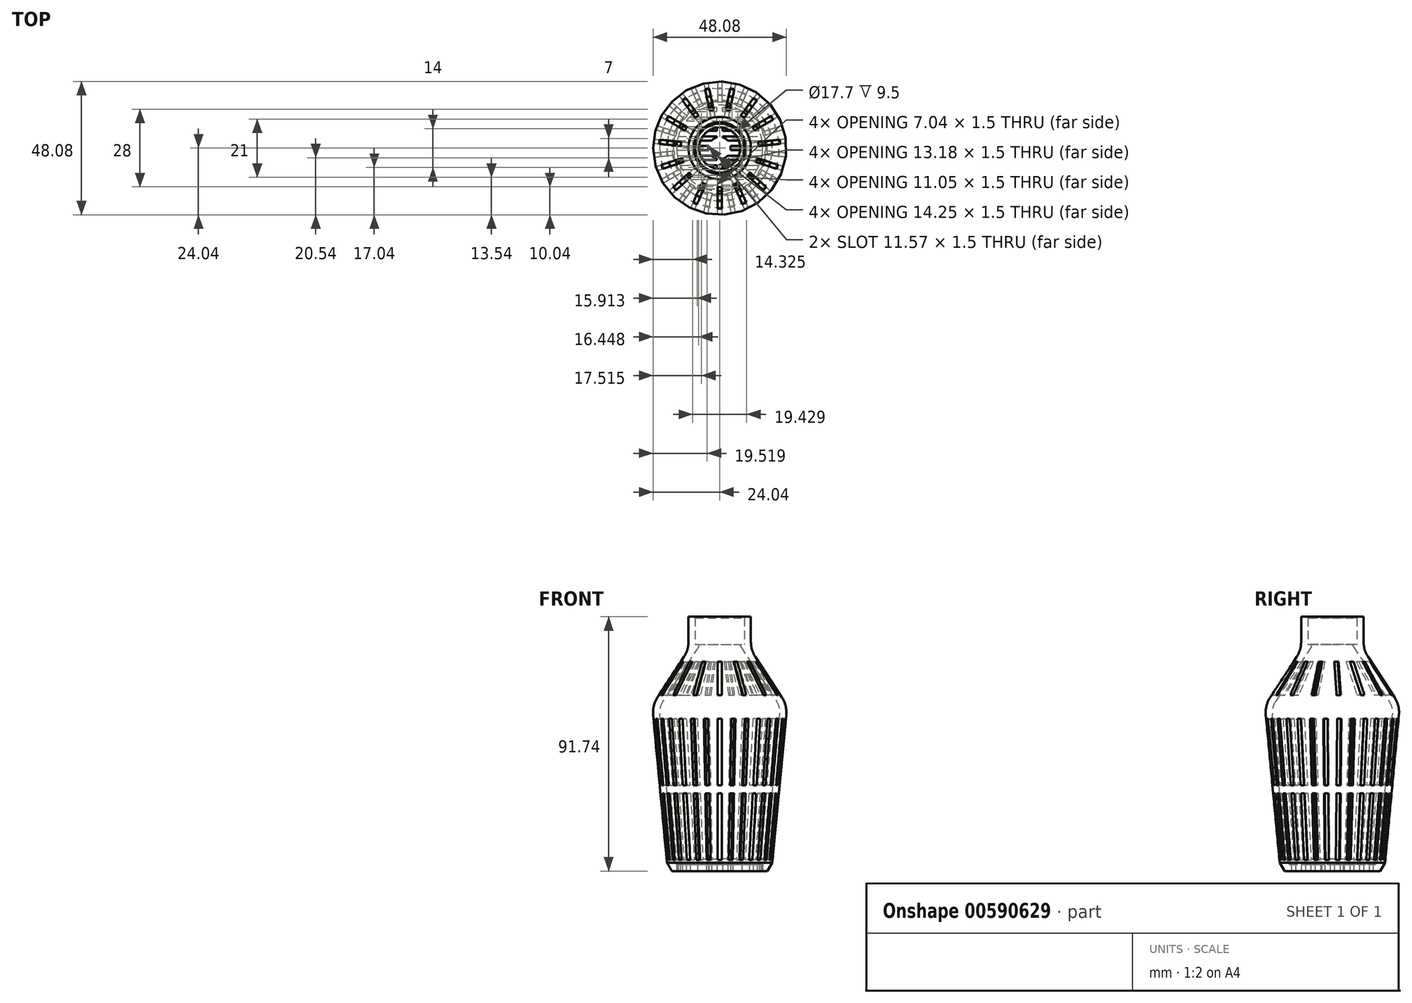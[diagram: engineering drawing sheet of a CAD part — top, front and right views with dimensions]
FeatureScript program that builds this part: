
annotation { "Feature Type Name" : "Feature", "Feature Type Description" : "" }
export const myFeature = defineFeature(function(context is Context, id is Id, definition is map)
    precondition{}
    {
        {
            var Q0;
            Q0=qCreatedBy(makeId("Front.planeOp"),FACE);
            var sketch = newSketch(context, id + "F0", { "sketchPlane" : qUnion([Q0])});
            skLineSegment(sketch, "E0", {"start": v(0, 0) * mm, "end": v(0, 100) * mm, "construction": true});
            skLineSegment(sketch, "E1", {"start": v(0, 0) * mm, "end": v(17.21, 0) * mm});
            skLineSegment(sketch, "E2", {"start": v(19, 3) * mm, "end": v(24, 56.26) * mm});
            skLineSegment(sketch, "E3", {"start": v(22.41, 62.66) * mm, "end": v(12.88, 77.24) * mm});
            skLineSegment(sketch, "E4", {"start": v(11.25, 82.72) * mm, "end": v(11.25, 91.74) * mm});
            skPoint(sketch, "E5.visualSharp", {"position": v(11.25, 79.74) * mm});
            skArc(sketch, "E5.filletArc", {"start": v(11.25, 82.72) * mm, "mid": v(11.67, 79.86) * mm, "end": v(12.88, 77.24) * mm});
            skPoint(sketch, "E6.visualSharp", {"position": v(24.33, 59.74) * mm});
            skArc(sketch, "E6.filletArc", {"start": v(24, 56.26) * mm, "mid": v(23.75, 59.6) * mm, "end": v(22.41, 62.66) * mm});
            skLineSegment(sketch, "E7", {"start": v(17.21, 0) * mm, "end": v(19, 3) * mm});
            skPoint(sketch, "E8.orphan", {"position": v(18.72, 0) * mm});
            skLineSegment(sketch, "E9.0", {"start": v(8.85, 81.74) * mm, "end": v(8.85, 91.74) * mm});
            skLineSegment(sketch, "E9.2", {"start": v(0, 2.4) * mm, "end": v(15.53, 2.4) * mm});
            skLineSegment(sketch, "E9.3", {"start": v(16.72, 4.4) * mm, "end": v(21.61, 56.48) * mm});
            skArc(sketch, "E9.4", {"start": v(21.61, 56.48) * mm, "mid": v(21.42, 59.02) * mm, "end": v(20.4, 61.35) * mm});
            skLineSegment(sketch, "E9.5", {"start": v(20.4, 61.35) * mm, "end": v(7.58, 80.96) * mm});
            skLineSegment(sketch, "E10", {"start": v(8.85, 91.74) * mm, "end": v(11.25, 91.74) * mm});
            skLineSegment(sketch, "E11", {"start": v(0, 2.4) * mm, "end": v(0, 0) * mm});
            skLineSegment(sketch, "E12", {"start": v(15.53, 2.4) * mm, "end": v(16.72, 4.4) * mm});
            skLineSegment(sketch, "E13", {"start": v(8.85, 81.74) * mm, "end": v(8, 81.74) * mm});
            skPoint(sketch, "E14.visualSharp", {"position": v(7.07, 81.74) * mm});
            skArc(sketch, "E14.filletArc", {"start": v(8, 81.74) * mm, "mid": v(7.56, 81.48) * mm, "end": v(7.58, 80.96) * mm});
            skSolve(sketch);
        }
        {
            var Q0;
            Q0 = qSketchRegion(id + "F0", true);
            var Q1;
            Q1=sQuery(id+"F0.wireOp",EDGE,"E0");
            revolve(context, id + "F1", {"entities" : qUnion([Q0]), "axis" : qUnion([Q1]), "revolveType" : RevolveType.FULL});
        }
        {
            var Q0;
            Q0=qCreatedBy(makeId("Front.planeOp"),FACE);
            var sketch = newSketch(context, id + "F2", { "sketchPlane" : qUnion([Q0])});
            skLineSegment(sketch, "E15", {"start": v(0, 0) * mm, "end": v(0, 100) * mm, "construction": true});
            skLineSegment(sketch, "E16.bottom", {"start": v(0.75, 4) * mm, "end": v(-0.75, 4) * mm});
            skLineSegment(sketch, "E16.top", {"start": v(0.75, 28) * mm, "end": v(-0.75, 28) * mm});
            skLineSegment(sketch, "E16.left", {"start": v(0.75, 4) * mm, "end": v(0.75, 28) * mm});
            skLineSegment(sketch, "E16.right", {"start": v(-0.75, 4) * mm, "end": v(-0.75, 28) * mm});
            skPoint(sketch, "E16.middle", {"position": v(0, 16) * mm});
            skLineSegment(sketch, "E17.bottom", {"start": v(0.75, 31) * mm, "end": v(-0.75, 31) * mm});
            skLineSegment(sketch, "E17.top", {"start": v(0.75, 55) * mm, "end": v(-0.75, 55) * mm});
            skLineSegment(sketch, "E17.left", {"start": v(0.75, 31) * mm, "end": v(0.75, 55) * mm});
            skLineSegment(sketch, "E17.right", {"start": v(-0.75, 31) * mm, "end": v(-0.75, 55) * mm});
            skPoint(sketch, "E17.middle", {"position": v(0, 43) * mm});
            skSolve(sketch);
        }
        {
            var Q0;
            Q0 = qSketchRegion(id + "F2", true);
            extrude(context, id + "F3", {"entities" : qUnion([Q0]), "oppositeDirection" : true, "depth" : 30 * mm, "offsetDistance" : 25 * mm});
        }
        {
            var Q0;
            Q0=makeQuery(id+"F3.opExtrude","SWEPT_BODY",BODY,{"disambiguationData":[OSD([sQuery(id+"F2.wireOp",EDGE,"E16.bottom"),sQuery(id+"F2.wireOp",EDGE,"E16.top"),sQuery(id+"F2.wireOp",EDGE,"E16.left"),sQuery(id+"F2.wireOp",EDGE,"E16.right")])]});
            var Q1;
            Q1=makeQuery(id+"F3.opExtrude","SWEPT_BODY",BODY,{"disambiguationData":[OSD([sQuery(id+"F2.wireOp",EDGE,"E17.bottom"),sQuery(id+"F2.wireOp",EDGE,"E17.top"),sQuery(id+"F2.wireOp",EDGE,"E17.left"),sQuery(id+"F2.wireOp",EDGE,"E17.right")])]});
            var Q2;
            Q2=makeQuery(id+"F3.opExtrude","SWEPT_BODY",BODY,{"disambiguationData":[OSD([sQuery(id+"F2.wireOp",EDGE,"CUWT8K6s-WbJc-WrEz-pjmn-ECC45j0oT72r.bottom"),sQuery(id+"F2.wireOp",EDGE,"CUWT8K6s-WbJc-WrEz-pjmn-ECC45j0oT72r.top"),sQuery(id+"F2.wireOp",EDGE,"CUWT8K6s-WbJc-WrEz-pjmn-ECC45j0oT72r.left"),sQuery(id+"F2.wireOp",EDGE,"CUWT8K6s-WbJc-WrEz-pjmn-ECC45j0oT72r.right")])]});
            var Q3;
            Q3=sQuery(id+"F0.wireOp",EDGE,"E0");
            circularPattern(context, id + "F4", {"entities" : qUnion([Q0, Q1, Q2]), "axis" : qUnion([Q3]), "angle" : 360 * degree, "instanceCount" : 30, "equalSpace" : true});
        }
        {
            var Q0;
            Q0=makeQuery(id+"F3.opExtrude","SWEPT_BODY",BODY,{"disambiguationData":[OSD([sQuery(id+"F2.wireOp",EDGE,"E16.bottom"),sQuery(id+"F2.wireOp",EDGE,"E16.top"),sQuery(id+"F2.wireOp",EDGE,"E16.left"),sQuery(id+"F2.wireOp",EDGE,"E16.right")])]});
            var Q1;
            Q1=makeQuery(id+"F3.opExtrude","SWEPT_BODY",BODY,{"disambiguationData":[OSD([sQuery(id+"F2.wireOp",EDGE,"E17.bottom"),sQuery(id+"F2.wireOp",EDGE,"E17.top"),sQuery(id+"F2.wireOp",EDGE,"E17.left"),sQuery(id+"F2.wireOp",EDGE,"E17.right")])]});
            var Q2;
            Q2=makeQuery(id+"F3.opExtrude","SWEPT_BODY",BODY,{"disambiguationData":[OSD([sQuery(id+"F2.wireOp",EDGE,"CUWT8K6s-WbJc-WrEz-pjmn-ECC45j0oT72r.bottom"),sQuery(id+"F2.wireOp",EDGE,"CUWT8K6s-WbJc-WrEz-pjmn-ECC45j0oT72r.top"),sQuery(id+"F2.wireOp",EDGE,"CUWT8K6s-WbJc-WrEz-pjmn-ECC45j0oT72r.left"),sQuery(id+"F2.wireOp",EDGE,"CUWT8K6s-WbJc-WrEz-pjmn-ECC45j0oT72r.right")])]});
            var Q3;
            Q3=makeQuery(id+"F4.opPattern","COPY",BODY,{"derivedFrom":makeQuery(id+"F3.opExtrude","SWEPT_BODY",BODY,{"disambiguationData":[OSD([sQuery(id+"F2.wireOp",EDGE,"E16.bottom"),sQuery(id+"F2.wireOp",EDGE,"E16.top"),sQuery(id+"F2.wireOp",EDGE,"E16.left"),sQuery(id+"F2.wireOp",EDGE,"E16.right")])]}),"instanceName":"1"});
            var Q4;
            Q4=makeQuery(id+"F4.opPattern","COPY",BODY,{"derivedFrom":makeQuery(id+"F3.opExtrude","SWEPT_BODY",BODY,{"disambiguationData":[OSD([sQuery(id+"F2.wireOp",EDGE,"E17.bottom"),sQuery(id+"F2.wireOp",EDGE,"E17.top"),sQuery(id+"F2.wireOp",EDGE,"E17.left"),sQuery(id+"F2.wireOp",EDGE,"E17.right")])]}),"instanceName":"1"});
            var Q5;
            Q5=makeQuery(id+"F4.opPattern","COPY",BODY,{"derivedFrom":makeQuery(id+"F3.opExtrude","SWEPT_BODY",BODY,{"disambiguationData":[OSD([sQuery(id+"F2.wireOp",EDGE,"CUWT8K6s-WbJc-WrEz-pjmn-ECC45j0oT72r.bottom"),sQuery(id+"F2.wireOp",EDGE,"CUWT8K6s-WbJc-WrEz-pjmn-ECC45j0oT72r.top"),sQuery(id+"F2.wireOp",EDGE,"CUWT8K6s-WbJc-WrEz-pjmn-ECC45j0oT72r.left"),sQuery(id+"F2.wireOp",EDGE,"CUWT8K6s-WbJc-WrEz-pjmn-ECC45j0oT72r.right")])]}),"instanceName":"1"});
            var Q6;
            Q6=makeQuery(id+"F4.opPattern","COPY",BODY,{"derivedFrom":makeQuery(id+"F3.opExtrude","SWEPT_BODY",BODY,{"disambiguationData":[OSD([sQuery(id+"F2.wireOp",EDGE,"E16.bottom"),sQuery(id+"F2.wireOp",EDGE,"E16.top"),sQuery(id+"F2.wireOp",EDGE,"E16.left"),sQuery(id+"F2.wireOp",EDGE,"E16.right")])]}),"instanceName":"2"});
            var Q7;
            Q7=makeQuery(id+"F4.opPattern","COPY",BODY,{"derivedFrom":makeQuery(id+"F3.opExtrude","SWEPT_BODY",BODY,{"disambiguationData":[OSD([sQuery(id+"F2.wireOp",EDGE,"E17.bottom"),sQuery(id+"F2.wireOp",EDGE,"E17.top"),sQuery(id+"F2.wireOp",EDGE,"E17.left"),sQuery(id+"F2.wireOp",EDGE,"E17.right")])]}),"instanceName":"2"});
            var Q8;
            Q8=makeQuery(id+"F4.opPattern","COPY",BODY,{"derivedFrom":makeQuery(id+"F3.opExtrude","SWEPT_BODY",BODY,{"disambiguationData":[OSD([sQuery(id+"F2.wireOp",EDGE,"CUWT8K6s-WbJc-WrEz-pjmn-ECC45j0oT72r.bottom"),sQuery(id+"F2.wireOp",EDGE,"CUWT8K6s-WbJc-WrEz-pjmn-ECC45j0oT72r.top"),sQuery(id+"F2.wireOp",EDGE,"CUWT8K6s-WbJc-WrEz-pjmn-ECC45j0oT72r.left"),sQuery(id+"F2.wireOp",EDGE,"CUWT8K6s-WbJc-WrEz-pjmn-ECC45j0oT72r.right")])]}),"instanceName":"2"});
            var Q9;
            Q9=makeQuery(id+"F4.opPattern","COPY",BODY,{"derivedFrom":makeQuery(id+"F3.opExtrude","SWEPT_BODY",BODY,{"disambiguationData":[OSD([sQuery(id+"F2.wireOp",EDGE,"E16.bottom"),sQuery(id+"F2.wireOp",EDGE,"E16.top"),sQuery(id+"F2.wireOp",EDGE,"E16.left"),sQuery(id+"F2.wireOp",EDGE,"E16.right")])]}),"instanceName":"3"});
            var Q10;
            Q10=makeQuery(id+"F4.opPattern","COPY",BODY,{"derivedFrom":makeQuery(id+"F3.opExtrude","SWEPT_BODY",BODY,{"disambiguationData":[OSD([sQuery(id+"F2.wireOp",EDGE,"E17.bottom"),sQuery(id+"F2.wireOp",EDGE,"E17.top"),sQuery(id+"F2.wireOp",EDGE,"E17.left"),sQuery(id+"F2.wireOp",EDGE,"E17.right")])]}),"instanceName":"3"});
            var Q11;
            Q11=makeQuery(id+"F4.opPattern","COPY",BODY,{"derivedFrom":makeQuery(id+"F3.opExtrude","SWEPT_BODY",BODY,{"disambiguationData":[OSD([sQuery(id+"F2.wireOp",EDGE,"CUWT8K6s-WbJc-WrEz-pjmn-ECC45j0oT72r.bottom"),sQuery(id+"F2.wireOp",EDGE,"CUWT8K6s-WbJc-WrEz-pjmn-ECC45j0oT72r.top"),sQuery(id+"F2.wireOp",EDGE,"CUWT8K6s-WbJc-WrEz-pjmn-ECC45j0oT72r.left"),sQuery(id+"F2.wireOp",EDGE,"CUWT8K6s-WbJc-WrEz-pjmn-ECC45j0oT72r.right")])]}),"instanceName":"3"});
            var Q12;
            Q12=makeQuery(id+"F4.opPattern","COPY",BODY,{"derivedFrom":makeQuery(id+"F3.opExtrude","SWEPT_BODY",BODY,{"disambiguationData":[OSD([sQuery(id+"F2.wireOp",EDGE,"E16.bottom"),sQuery(id+"F2.wireOp",EDGE,"E16.top"),sQuery(id+"F2.wireOp",EDGE,"E16.left"),sQuery(id+"F2.wireOp",EDGE,"E16.right")])]}),"instanceName":"4"});
            var Q13;
            Q13=makeQuery(id+"F4.opPattern","COPY",BODY,{"derivedFrom":makeQuery(id+"F3.opExtrude","SWEPT_BODY",BODY,{"disambiguationData":[OSD([sQuery(id+"F2.wireOp",EDGE,"E17.bottom"),sQuery(id+"F2.wireOp",EDGE,"E17.top"),sQuery(id+"F2.wireOp",EDGE,"E17.left"),sQuery(id+"F2.wireOp",EDGE,"E17.right")])]}),"instanceName":"4"});
            var Q14;
            Q14=makeQuery(id+"F4.opPattern","COPY",BODY,{"derivedFrom":makeQuery(id+"F3.opExtrude","SWEPT_BODY",BODY,{"disambiguationData":[OSD([sQuery(id+"F2.wireOp",EDGE,"CUWT8K6s-WbJc-WrEz-pjmn-ECC45j0oT72r.bottom"),sQuery(id+"F2.wireOp",EDGE,"CUWT8K6s-WbJc-WrEz-pjmn-ECC45j0oT72r.top"),sQuery(id+"F2.wireOp",EDGE,"CUWT8K6s-WbJc-WrEz-pjmn-ECC45j0oT72r.left"),sQuery(id+"F2.wireOp",EDGE,"CUWT8K6s-WbJc-WrEz-pjmn-ECC45j0oT72r.right")])]}),"instanceName":"4"});
            var Q15;
            Q15=makeQuery(id+"F4.opPattern","COPY",BODY,{"derivedFrom":makeQuery(id+"F3.opExtrude","SWEPT_BODY",BODY,{"disambiguationData":[OSD([sQuery(id+"F2.wireOp",EDGE,"E16.bottom"),sQuery(id+"F2.wireOp",EDGE,"E16.top"),sQuery(id+"F2.wireOp",EDGE,"E16.left"),sQuery(id+"F2.wireOp",EDGE,"E16.right")])]}),"instanceName":"5"});
            var Q16;
            Q16=makeQuery(id+"F4.opPattern","COPY",BODY,{"derivedFrom":makeQuery(id+"F3.opExtrude","SWEPT_BODY",BODY,{"disambiguationData":[OSD([sQuery(id+"F2.wireOp",EDGE,"E17.bottom"),sQuery(id+"F2.wireOp",EDGE,"E17.top"),sQuery(id+"F2.wireOp",EDGE,"E17.left"),sQuery(id+"F2.wireOp",EDGE,"E17.right")])]}),"instanceName":"5"});
            var Q17;
            Q17=makeQuery(id+"F4.opPattern","COPY",BODY,{"derivedFrom":makeQuery(id+"F3.opExtrude","SWEPT_BODY",BODY,{"disambiguationData":[OSD([sQuery(id+"F2.wireOp",EDGE,"CUWT8K6s-WbJc-WrEz-pjmn-ECC45j0oT72r.bottom"),sQuery(id+"F2.wireOp",EDGE,"CUWT8K6s-WbJc-WrEz-pjmn-ECC45j0oT72r.top"),sQuery(id+"F2.wireOp",EDGE,"CUWT8K6s-WbJc-WrEz-pjmn-ECC45j0oT72r.left"),sQuery(id+"F2.wireOp",EDGE,"CUWT8K6s-WbJc-WrEz-pjmn-ECC45j0oT72r.right")])]}),"instanceName":"5"});
            var Q18;
            Q18=makeQuery(id+"F4.opPattern","COPY",BODY,{"derivedFrom":makeQuery(id+"F3.opExtrude","SWEPT_BODY",BODY,{"disambiguationData":[OSD([sQuery(id+"F2.wireOp",EDGE,"E16.bottom"),sQuery(id+"F2.wireOp",EDGE,"E16.top"),sQuery(id+"F2.wireOp",EDGE,"E16.left"),sQuery(id+"F2.wireOp",EDGE,"E16.right")])]}),"instanceName":"6"});
            var Q19;
            Q19=makeQuery(id+"F4.opPattern","COPY",BODY,{"derivedFrom":makeQuery(id+"F3.opExtrude","SWEPT_BODY",BODY,{"disambiguationData":[OSD([sQuery(id+"F2.wireOp",EDGE,"E17.bottom"),sQuery(id+"F2.wireOp",EDGE,"E17.top"),sQuery(id+"F2.wireOp",EDGE,"E17.left"),sQuery(id+"F2.wireOp",EDGE,"E17.right")])]}),"instanceName":"6"});
            var Q20;
            Q20=makeQuery(id+"F4.opPattern","COPY",BODY,{"derivedFrom":makeQuery(id+"F3.opExtrude","SWEPT_BODY",BODY,{"disambiguationData":[OSD([sQuery(id+"F2.wireOp",EDGE,"CUWT8K6s-WbJc-WrEz-pjmn-ECC45j0oT72r.bottom"),sQuery(id+"F2.wireOp",EDGE,"CUWT8K6s-WbJc-WrEz-pjmn-ECC45j0oT72r.top"),sQuery(id+"F2.wireOp",EDGE,"CUWT8K6s-WbJc-WrEz-pjmn-ECC45j0oT72r.left"),sQuery(id+"F2.wireOp",EDGE,"CUWT8K6s-WbJc-WrEz-pjmn-ECC45j0oT72r.right")])]}),"instanceName":"6"});
            var Q21;
            Q21=makeQuery(id+"F4.opPattern","COPY",BODY,{"derivedFrom":makeQuery(id+"F3.opExtrude","SWEPT_BODY",BODY,{"disambiguationData":[OSD([sQuery(id+"F2.wireOp",EDGE,"E16.bottom"),sQuery(id+"F2.wireOp",EDGE,"E16.top"),sQuery(id+"F2.wireOp",EDGE,"E16.left"),sQuery(id+"F2.wireOp",EDGE,"E16.right")])]}),"instanceName":"7"});
            var Q22;
            Q22=makeQuery(id+"F4.opPattern","COPY",BODY,{"derivedFrom":makeQuery(id+"F3.opExtrude","SWEPT_BODY",BODY,{"disambiguationData":[OSD([sQuery(id+"F2.wireOp",EDGE,"E17.bottom"),sQuery(id+"F2.wireOp",EDGE,"E17.top"),sQuery(id+"F2.wireOp",EDGE,"E17.left"),sQuery(id+"F2.wireOp",EDGE,"E17.right")])]}),"instanceName":"7"});
            var Q23;
            Q23=makeQuery(id+"F4.opPattern","COPY",BODY,{"derivedFrom":makeQuery(id+"F3.opExtrude","SWEPT_BODY",BODY,{"disambiguationData":[OSD([sQuery(id+"F2.wireOp",EDGE,"CUWT8K6s-WbJc-WrEz-pjmn-ECC45j0oT72r.bottom"),sQuery(id+"F2.wireOp",EDGE,"CUWT8K6s-WbJc-WrEz-pjmn-ECC45j0oT72r.top"),sQuery(id+"F2.wireOp",EDGE,"CUWT8K6s-WbJc-WrEz-pjmn-ECC45j0oT72r.left"),sQuery(id+"F2.wireOp",EDGE,"CUWT8K6s-WbJc-WrEz-pjmn-ECC45j0oT72r.right")])]}),"instanceName":"7"});
            var Q24;
            Q24=makeQuery(id+"F4.opPattern","COPY",BODY,{"derivedFrom":makeQuery(id+"F3.opExtrude","SWEPT_BODY",BODY,{"disambiguationData":[OSD([sQuery(id+"F2.wireOp",EDGE,"E16.bottom"),sQuery(id+"F2.wireOp",EDGE,"E16.top"),sQuery(id+"F2.wireOp",EDGE,"E16.left"),sQuery(id+"F2.wireOp",EDGE,"E16.right")])]}),"instanceName":"8"});
            var Q25;
            Q25=makeQuery(id+"F4.opPattern","COPY",BODY,{"derivedFrom":makeQuery(id+"F3.opExtrude","SWEPT_BODY",BODY,{"disambiguationData":[OSD([sQuery(id+"F2.wireOp",EDGE,"E17.bottom"),sQuery(id+"F2.wireOp",EDGE,"E17.top"),sQuery(id+"F2.wireOp",EDGE,"E17.left"),sQuery(id+"F2.wireOp",EDGE,"E17.right")])]}),"instanceName":"8"});
            var Q26;
            Q26=makeQuery(id+"F4.opPattern","COPY",BODY,{"derivedFrom":makeQuery(id+"F3.opExtrude","SWEPT_BODY",BODY,{"disambiguationData":[OSD([sQuery(id+"F2.wireOp",EDGE,"CUWT8K6s-WbJc-WrEz-pjmn-ECC45j0oT72r.bottom"),sQuery(id+"F2.wireOp",EDGE,"CUWT8K6s-WbJc-WrEz-pjmn-ECC45j0oT72r.top"),sQuery(id+"F2.wireOp",EDGE,"CUWT8K6s-WbJc-WrEz-pjmn-ECC45j0oT72r.left"),sQuery(id+"F2.wireOp",EDGE,"CUWT8K6s-WbJc-WrEz-pjmn-ECC45j0oT72r.right")])]}),"instanceName":"8"});
            var Q27;
            Q27=makeQuery(id+"F4.opPattern","COPY",BODY,{"derivedFrom":makeQuery(id+"F3.opExtrude","SWEPT_BODY",BODY,{"disambiguationData":[OSD([sQuery(id+"F2.wireOp",EDGE,"E16.bottom"),sQuery(id+"F2.wireOp",EDGE,"E16.top"),sQuery(id+"F2.wireOp",EDGE,"E16.left"),sQuery(id+"F2.wireOp",EDGE,"E16.right")])]}),"instanceName":"9"});
            var Q28;
            Q28=makeQuery(id+"F4.opPattern","COPY",BODY,{"derivedFrom":makeQuery(id+"F3.opExtrude","SWEPT_BODY",BODY,{"disambiguationData":[OSD([sQuery(id+"F2.wireOp",EDGE,"E17.bottom"),sQuery(id+"F2.wireOp",EDGE,"E17.top"),sQuery(id+"F2.wireOp",EDGE,"E17.left"),sQuery(id+"F2.wireOp",EDGE,"E17.right")])]}),"instanceName":"9"});
            var Q29;
            Q29=makeQuery(id+"F4.opPattern","COPY",BODY,{"derivedFrom":makeQuery(id+"F3.opExtrude","SWEPT_BODY",BODY,{"disambiguationData":[OSD([sQuery(id+"F2.wireOp",EDGE,"CUWT8K6s-WbJc-WrEz-pjmn-ECC45j0oT72r.bottom"),sQuery(id+"F2.wireOp",EDGE,"CUWT8K6s-WbJc-WrEz-pjmn-ECC45j0oT72r.top"),sQuery(id+"F2.wireOp",EDGE,"CUWT8K6s-WbJc-WrEz-pjmn-ECC45j0oT72r.left"),sQuery(id+"F2.wireOp",EDGE,"CUWT8K6s-WbJc-WrEz-pjmn-ECC45j0oT72r.right")])]}),"instanceName":"9"});
            var Q30;
            Q30=makeQuery(id+"F4.opPattern","COPY",BODY,{"derivedFrom":makeQuery(id+"F3.opExtrude","SWEPT_BODY",BODY,{"disambiguationData":[OSD([sQuery(id+"F2.wireOp",EDGE,"E16.bottom"),sQuery(id+"F2.wireOp",EDGE,"E16.top"),sQuery(id+"F2.wireOp",EDGE,"E16.left"),sQuery(id+"F2.wireOp",EDGE,"E16.right")])]}),"instanceName":"10"});
            var Q31;
            Q31=makeQuery(id+"F4.opPattern","COPY",BODY,{"derivedFrom":makeQuery(id+"F3.opExtrude","SWEPT_BODY",BODY,{"disambiguationData":[OSD([sQuery(id+"F2.wireOp",EDGE,"E17.bottom"),sQuery(id+"F2.wireOp",EDGE,"E17.top"),sQuery(id+"F2.wireOp",EDGE,"E17.left"),sQuery(id+"F2.wireOp",EDGE,"E17.right")])]}),"instanceName":"10"});
            var Q32;
            Q32=makeQuery(id+"F4.opPattern","COPY",BODY,{"derivedFrom":makeQuery(id+"F3.opExtrude","SWEPT_BODY",BODY,{"disambiguationData":[OSD([sQuery(id+"F2.wireOp",EDGE,"CUWT8K6s-WbJc-WrEz-pjmn-ECC45j0oT72r.bottom"),sQuery(id+"F2.wireOp",EDGE,"CUWT8K6s-WbJc-WrEz-pjmn-ECC45j0oT72r.top"),sQuery(id+"F2.wireOp",EDGE,"CUWT8K6s-WbJc-WrEz-pjmn-ECC45j0oT72r.left"),sQuery(id+"F2.wireOp",EDGE,"CUWT8K6s-WbJc-WrEz-pjmn-ECC45j0oT72r.right")])]}),"instanceName":"10"});
            var Q33;
            Q33=makeQuery(id+"F4.opPattern","COPY",BODY,{"derivedFrom":makeQuery(id+"F3.opExtrude","SWEPT_BODY",BODY,{"disambiguationData":[OSD([sQuery(id+"F2.wireOp",EDGE,"E16.bottom"),sQuery(id+"F2.wireOp",EDGE,"E16.top"),sQuery(id+"F2.wireOp",EDGE,"E16.left"),sQuery(id+"F2.wireOp",EDGE,"E16.right")])]}),"instanceName":"11"});
            var Q34;
            Q34=makeQuery(id+"F4.opPattern","COPY",BODY,{"derivedFrom":makeQuery(id+"F3.opExtrude","SWEPT_BODY",BODY,{"disambiguationData":[OSD([sQuery(id+"F2.wireOp",EDGE,"E17.bottom"),sQuery(id+"F2.wireOp",EDGE,"E17.top"),sQuery(id+"F2.wireOp",EDGE,"E17.left"),sQuery(id+"F2.wireOp",EDGE,"E17.right")])]}),"instanceName":"11"});
            var Q35;
            Q35=makeQuery(id+"F4.opPattern","COPY",BODY,{"derivedFrom":makeQuery(id+"F3.opExtrude","SWEPT_BODY",BODY,{"disambiguationData":[OSD([sQuery(id+"F2.wireOp",EDGE,"CUWT8K6s-WbJc-WrEz-pjmn-ECC45j0oT72r.bottom"),sQuery(id+"F2.wireOp",EDGE,"CUWT8K6s-WbJc-WrEz-pjmn-ECC45j0oT72r.top"),sQuery(id+"F2.wireOp",EDGE,"CUWT8K6s-WbJc-WrEz-pjmn-ECC45j0oT72r.left"),sQuery(id+"F2.wireOp",EDGE,"CUWT8K6s-WbJc-WrEz-pjmn-ECC45j0oT72r.right")])]}),"instanceName":"11"});
            var Q36;
            Q36=makeQuery(id+"F4.opPattern","COPY",BODY,{"derivedFrom":makeQuery(id+"F3.opExtrude","SWEPT_BODY",BODY,{"disambiguationData":[OSD([sQuery(id+"F2.wireOp",EDGE,"E16.bottom"),sQuery(id+"F2.wireOp",EDGE,"E16.top"),sQuery(id+"F2.wireOp",EDGE,"E16.left"),sQuery(id+"F2.wireOp",EDGE,"E16.right")])]}),"instanceName":"12"});
            var Q37;
            Q37=makeQuery(id+"F4.opPattern","COPY",BODY,{"derivedFrom":makeQuery(id+"F3.opExtrude","SWEPT_BODY",BODY,{"disambiguationData":[OSD([sQuery(id+"F2.wireOp",EDGE,"E17.bottom"),sQuery(id+"F2.wireOp",EDGE,"E17.top"),sQuery(id+"F2.wireOp",EDGE,"E17.left"),sQuery(id+"F2.wireOp",EDGE,"E17.right")])]}),"instanceName":"12"});
            var Q38;
            Q38=makeQuery(id+"F4.opPattern","COPY",BODY,{"derivedFrom":makeQuery(id+"F3.opExtrude","SWEPT_BODY",BODY,{"disambiguationData":[OSD([sQuery(id+"F2.wireOp",EDGE,"CUWT8K6s-WbJc-WrEz-pjmn-ECC45j0oT72r.bottom"),sQuery(id+"F2.wireOp",EDGE,"CUWT8K6s-WbJc-WrEz-pjmn-ECC45j0oT72r.top"),sQuery(id+"F2.wireOp",EDGE,"CUWT8K6s-WbJc-WrEz-pjmn-ECC45j0oT72r.left"),sQuery(id+"F2.wireOp",EDGE,"CUWT8K6s-WbJc-WrEz-pjmn-ECC45j0oT72r.right")])]}),"instanceName":"12"});
            var Q39;
            Q39=makeQuery(id+"F4.opPattern","COPY",BODY,{"derivedFrom":makeQuery(id+"F3.opExtrude","SWEPT_BODY",BODY,{"disambiguationData":[OSD([sQuery(id+"F2.wireOp",EDGE,"E16.bottom"),sQuery(id+"F2.wireOp",EDGE,"E16.top"),sQuery(id+"F2.wireOp",EDGE,"E16.left"),sQuery(id+"F2.wireOp",EDGE,"E16.right")])]}),"instanceName":"13"});
            var Q40;
            Q40=makeQuery(id+"F4.opPattern","COPY",BODY,{"derivedFrom":makeQuery(id+"F3.opExtrude","SWEPT_BODY",BODY,{"disambiguationData":[OSD([sQuery(id+"F2.wireOp",EDGE,"E17.bottom"),sQuery(id+"F2.wireOp",EDGE,"E17.top"),sQuery(id+"F2.wireOp",EDGE,"E17.left"),sQuery(id+"F2.wireOp",EDGE,"E17.right")])]}),"instanceName":"13"});
            var Q41;
            Q41=makeQuery(id+"F4.opPattern","COPY",BODY,{"derivedFrom":makeQuery(id+"F3.opExtrude","SWEPT_BODY",BODY,{"disambiguationData":[OSD([sQuery(id+"F2.wireOp",EDGE,"CUWT8K6s-WbJc-WrEz-pjmn-ECC45j0oT72r.bottom"),sQuery(id+"F2.wireOp",EDGE,"CUWT8K6s-WbJc-WrEz-pjmn-ECC45j0oT72r.top"),sQuery(id+"F2.wireOp",EDGE,"CUWT8K6s-WbJc-WrEz-pjmn-ECC45j0oT72r.left"),sQuery(id+"F2.wireOp",EDGE,"CUWT8K6s-WbJc-WrEz-pjmn-ECC45j0oT72r.right")])]}),"instanceName":"13"});
            var Q42;
            Q42=makeQuery(id+"F4.opPattern","COPY",BODY,{"derivedFrom":makeQuery(id+"F3.opExtrude","SWEPT_BODY",BODY,{"disambiguationData":[OSD([sQuery(id+"F2.wireOp",EDGE,"E16.bottom"),sQuery(id+"F2.wireOp",EDGE,"E16.top"),sQuery(id+"F2.wireOp",EDGE,"E16.left"),sQuery(id+"F2.wireOp",EDGE,"E16.right")])]}),"instanceName":"14"});
            var Q43;
            Q43=makeQuery(id+"F4.opPattern","COPY",BODY,{"derivedFrom":makeQuery(id+"F3.opExtrude","SWEPT_BODY",BODY,{"disambiguationData":[OSD([sQuery(id+"F2.wireOp",EDGE,"E17.bottom"),sQuery(id+"F2.wireOp",EDGE,"E17.top"),sQuery(id+"F2.wireOp",EDGE,"E17.left"),sQuery(id+"F2.wireOp",EDGE,"E17.right")])]}),"instanceName":"14"});
            var Q44;
            Q44=makeQuery(id+"F4.opPattern","COPY",BODY,{"derivedFrom":makeQuery(id+"F3.opExtrude","SWEPT_BODY",BODY,{"disambiguationData":[OSD([sQuery(id+"F2.wireOp",EDGE,"CUWT8K6s-WbJc-WrEz-pjmn-ECC45j0oT72r.bottom"),sQuery(id+"F2.wireOp",EDGE,"CUWT8K6s-WbJc-WrEz-pjmn-ECC45j0oT72r.top"),sQuery(id+"F2.wireOp",EDGE,"CUWT8K6s-WbJc-WrEz-pjmn-ECC45j0oT72r.left"),sQuery(id+"F2.wireOp",EDGE,"CUWT8K6s-WbJc-WrEz-pjmn-ECC45j0oT72r.right")])]}),"instanceName":"14"});
            var Q45;
            Q45=makeQuery(id+"F4.opPattern","COPY",BODY,{"derivedFrom":makeQuery(id+"F3.opExtrude","SWEPT_BODY",BODY,{"disambiguationData":[OSD([sQuery(id+"F2.wireOp",EDGE,"E16.bottom"),sQuery(id+"F2.wireOp",EDGE,"E16.top"),sQuery(id+"F2.wireOp",EDGE,"E16.left"),sQuery(id+"F2.wireOp",EDGE,"E16.right")])]}),"instanceName":"15"});
            var Q46;
            Q46=makeQuery(id+"F4.opPattern","COPY",BODY,{"derivedFrom":makeQuery(id+"F3.opExtrude","SWEPT_BODY",BODY,{"disambiguationData":[OSD([sQuery(id+"F2.wireOp",EDGE,"E17.bottom"),sQuery(id+"F2.wireOp",EDGE,"E17.top"),sQuery(id+"F2.wireOp",EDGE,"E17.left"),sQuery(id+"F2.wireOp",EDGE,"E17.right")])]}),"instanceName":"15"});
            var Q47;
            Q47=makeQuery(id+"F4.opPattern","COPY",BODY,{"derivedFrom":makeQuery(id+"F3.opExtrude","SWEPT_BODY",BODY,{"disambiguationData":[OSD([sQuery(id+"F2.wireOp",EDGE,"CUWT8K6s-WbJc-WrEz-pjmn-ECC45j0oT72r.bottom"),sQuery(id+"F2.wireOp",EDGE,"CUWT8K6s-WbJc-WrEz-pjmn-ECC45j0oT72r.top"),sQuery(id+"F2.wireOp",EDGE,"CUWT8K6s-WbJc-WrEz-pjmn-ECC45j0oT72r.left"),sQuery(id+"F2.wireOp",EDGE,"CUWT8K6s-WbJc-WrEz-pjmn-ECC45j0oT72r.right")])]}),"instanceName":"15"});
            var Q48;
            Q48=makeQuery(id+"F4.opPattern","COPY",BODY,{"derivedFrom":makeQuery(id+"F3.opExtrude","SWEPT_BODY",BODY,{"disambiguationData":[OSD([sQuery(id+"F2.wireOp",EDGE,"E16.bottom"),sQuery(id+"F2.wireOp",EDGE,"E16.top"),sQuery(id+"F2.wireOp",EDGE,"E16.left"),sQuery(id+"F2.wireOp",EDGE,"E16.right")])]}),"instanceName":"16"});
            var Q49;
            Q49=makeQuery(id+"F4.opPattern","COPY",BODY,{"derivedFrom":makeQuery(id+"F3.opExtrude","SWEPT_BODY",BODY,{"disambiguationData":[OSD([sQuery(id+"F2.wireOp",EDGE,"E17.bottom"),sQuery(id+"F2.wireOp",EDGE,"E17.top"),sQuery(id+"F2.wireOp",EDGE,"E17.left"),sQuery(id+"F2.wireOp",EDGE,"E17.right")])]}),"instanceName":"16"});
            var Q50;
            Q50=makeQuery(id+"F4.opPattern","COPY",BODY,{"derivedFrom":makeQuery(id+"F3.opExtrude","SWEPT_BODY",BODY,{"disambiguationData":[OSD([sQuery(id+"F2.wireOp",EDGE,"CUWT8K6s-WbJc-WrEz-pjmn-ECC45j0oT72r.bottom"),sQuery(id+"F2.wireOp",EDGE,"CUWT8K6s-WbJc-WrEz-pjmn-ECC45j0oT72r.top"),sQuery(id+"F2.wireOp",EDGE,"CUWT8K6s-WbJc-WrEz-pjmn-ECC45j0oT72r.left"),sQuery(id+"F2.wireOp",EDGE,"CUWT8K6s-WbJc-WrEz-pjmn-ECC45j0oT72r.right")])]}),"instanceName":"16"});
            var Q51;
            Q51=makeQuery(id+"F4.opPattern","COPY",BODY,{"derivedFrom":makeQuery(id+"F3.opExtrude","SWEPT_BODY",BODY,{"disambiguationData":[OSD([sQuery(id+"F2.wireOp",EDGE,"E16.bottom"),sQuery(id+"F2.wireOp",EDGE,"E16.top"),sQuery(id+"F2.wireOp",EDGE,"E16.left"),sQuery(id+"F2.wireOp",EDGE,"E16.right")])]}),"instanceName":"17"});
            var Q52;
            Q52=makeQuery(id+"F4.opPattern","COPY",BODY,{"derivedFrom":makeQuery(id+"F3.opExtrude","SWEPT_BODY",BODY,{"disambiguationData":[OSD([sQuery(id+"F2.wireOp",EDGE,"E17.bottom"),sQuery(id+"F2.wireOp",EDGE,"E17.top"),sQuery(id+"F2.wireOp",EDGE,"E17.left"),sQuery(id+"F2.wireOp",EDGE,"E17.right")])]}),"instanceName":"17"});
            var Q53;
            Q53=makeQuery(id+"F4.opPattern","COPY",BODY,{"derivedFrom":makeQuery(id+"F3.opExtrude","SWEPT_BODY",BODY,{"disambiguationData":[OSD([sQuery(id+"F2.wireOp",EDGE,"CUWT8K6s-WbJc-WrEz-pjmn-ECC45j0oT72r.bottom"),sQuery(id+"F2.wireOp",EDGE,"CUWT8K6s-WbJc-WrEz-pjmn-ECC45j0oT72r.top"),sQuery(id+"F2.wireOp",EDGE,"CUWT8K6s-WbJc-WrEz-pjmn-ECC45j0oT72r.left"),sQuery(id+"F2.wireOp",EDGE,"CUWT8K6s-WbJc-WrEz-pjmn-ECC45j0oT72r.right")])]}),"instanceName":"17"});
            var Q54;
            Q54=makeQuery(id+"F4.opPattern","COPY",BODY,{"derivedFrom":makeQuery(id+"F3.opExtrude","SWEPT_BODY",BODY,{"disambiguationData":[OSD([sQuery(id+"F2.wireOp",EDGE,"E16.bottom"),sQuery(id+"F2.wireOp",EDGE,"E16.top"),sQuery(id+"F2.wireOp",EDGE,"E16.left"),sQuery(id+"F2.wireOp",EDGE,"E16.right")])]}),"instanceName":"18"});
            var Q55;
            Q55=makeQuery(id+"F4.opPattern","COPY",BODY,{"derivedFrom":makeQuery(id+"F3.opExtrude","SWEPT_BODY",BODY,{"disambiguationData":[OSD([sQuery(id+"F2.wireOp",EDGE,"E17.bottom"),sQuery(id+"F2.wireOp",EDGE,"E17.top"),sQuery(id+"F2.wireOp",EDGE,"E17.left"),sQuery(id+"F2.wireOp",EDGE,"E17.right")])]}),"instanceName":"18"});
            var Q56;
            Q56=makeQuery(id+"F4.opPattern","COPY",BODY,{"derivedFrom":makeQuery(id+"F3.opExtrude","SWEPT_BODY",BODY,{"disambiguationData":[OSD([sQuery(id+"F2.wireOp",EDGE,"CUWT8K6s-WbJc-WrEz-pjmn-ECC45j0oT72r.bottom"),sQuery(id+"F2.wireOp",EDGE,"CUWT8K6s-WbJc-WrEz-pjmn-ECC45j0oT72r.top"),sQuery(id+"F2.wireOp",EDGE,"CUWT8K6s-WbJc-WrEz-pjmn-ECC45j0oT72r.left"),sQuery(id+"F2.wireOp",EDGE,"CUWT8K6s-WbJc-WrEz-pjmn-ECC45j0oT72r.right")])]}),"instanceName":"18"});
            var Q57;
            Q57=makeQuery(id+"F4.opPattern","COPY",BODY,{"derivedFrom":makeQuery(id+"F3.opExtrude","SWEPT_BODY",BODY,{"disambiguationData":[OSD([sQuery(id+"F2.wireOp",EDGE,"E16.bottom"),sQuery(id+"F2.wireOp",EDGE,"E16.top"),sQuery(id+"F2.wireOp",EDGE,"E16.left"),sQuery(id+"F2.wireOp",EDGE,"E16.right")])]}),"instanceName":"19"});
            var Q58;
            Q58=makeQuery(id+"F4.opPattern","COPY",BODY,{"derivedFrom":makeQuery(id+"F3.opExtrude","SWEPT_BODY",BODY,{"disambiguationData":[OSD([sQuery(id+"F2.wireOp",EDGE,"E17.bottom"),sQuery(id+"F2.wireOp",EDGE,"E17.top"),sQuery(id+"F2.wireOp",EDGE,"E17.left"),sQuery(id+"F2.wireOp",EDGE,"E17.right")])]}),"instanceName":"19"});
            var Q59;
            Q59=makeQuery(id+"F4.opPattern","COPY",BODY,{"derivedFrom":makeQuery(id+"F3.opExtrude","SWEPT_BODY",BODY,{"disambiguationData":[OSD([sQuery(id+"F2.wireOp",EDGE,"CUWT8K6s-WbJc-WrEz-pjmn-ECC45j0oT72r.bottom"),sQuery(id+"F2.wireOp",EDGE,"CUWT8K6s-WbJc-WrEz-pjmn-ECC45j0oT72r.top"),sQuery(id+"F2.wireOp",EDGE,"CUWT8K6s-WbJc-WrEz-pjmn-ECC45j0oT72r.left"),sQuery(id+"F2.wireOp",EDGE,"CUWT8K6s-WbJc-WrEz-pjmn-ECC45j0oT72r.right")])]}),"instanceName":"19"});
            var Q60;
            Q60=makeQuery(id+"F4.opPattern","COPY",BODY,{"derivedFrom":makeQuery(id+"F3.opExtrude","SWEPT_BODY",BODY,{"disambiguationData":[OSD([sQuery(id+"F2.wireOp",EDGE,"E16.bottom"),sQuery(id+"F2.wireOp",EDGE,"E16.top"),sQuery(id+"F2.wireOp",EDGE,"E16.left"),sQuery(id+"F2.wireOp",EDGE,"E16.right")])]}),"instanceName":"20"});
            var Q61;
            Q61=makeQuery(id+"F4.opPattern","COPY",BODY,{"derivedFrom":makeQuery(id+"F3.opExtrude","SWEPT_BODY",BODY,{"disambiguationData":[OSD([sQuery(id+"F2.wireOp",EDGE,"E17.bottom"),sQuery(id+"F2.wireOp",EDGE,"E17.top"),sQuery(id+"F2.wireOp",EDGE,"E17.left"),sQuery(id+"F2.wireOp",EDGE,"E17.right")])]}),"instanceName":"20"});
            var Q62;
            Q62=makeQuery(id+"F4.opPattern","COPY",BODY,{"derivedFrom":makeQuery(id+"F3.opExtrude","SWEPT_BODY",BODY,{"disambiguationData":[OSD([sQuery(id+"F2.wireOp",EDGE,"CUWT8K6s-WbJc-WrEz-pjmn-ECC45j0oT72r.bottom"),sQuery(id+"F2.wireOp",EDGE,"CUWT8K6s-WbJc-WrEz-pjmn-ECC45j0oT72r.top"),sQuery(id+"F2.wireOp",EDGE,"CUWT8K6s-WbJc-WrEz-pjmn-ECC45j0oT72r.left"),sQuery(id+"F2.wireOp",EDGE,"CUWT8K6s-WbJc-WrEz-pjmn-ECC45j0oT72r.right")])]}),"instanceName":"20"});
            var Q63;
            Q63=makeQuery(id+"F4.opPattern","COPY",BODY,{"derivedFrom":makeQuery(id+"F3.opExtrude","SWEPT_BODY",BODY,{"disambiguationData":[OSD([sQuery(id+"F2.wireOp",EDGE,"E16.bottom"),sQuery(id+"F2.wireOp",EDGE,"E16.top"),sQuery(id+"F2.wireOp",EDGE,"E16.left"),sQuery(id+"F2.wireOp",EDGE,"E16.right")])]}),"instanceName":"21"});
            var Q64;
            Q64=makeQuery(id+"F4.opPattern","COPY",BODY,{"derivedFrom":makeQuery(id+"F3.opExtrude","SWEPT_BODY",BODY,{"disambiguationData":[OSD([sQuery(id+"F2.wireOp",EDGE,"E17.bottom"),sQuery(id+"F2.wireOp",EDGE,"E17.top"),sQuery(id+"F2.wireOp",EDGE,"E17.left"),sQuery(id+"F2.wireOp",EDGE,"E17.right")])]}),"instanceName":"21"});
            var Q65;
            Q65=makeQuery(id+"F4.opPattern","COPY",BODY,{"derivedFrom":makeQuery(id+"F3.opExtrude","SWEPT_BODY",BODY,{"disambiguationData":[OSD([sQuery(id+"F2.wireOp",EDGE,"CUWT8K6s-WbJc-WrEz-pjmn-ECC45j0oT72r.bottom"),sQuery(id+"F2.wireOp",EDGE,"CUWT8K6s-WbJc-WrEz-pjmn-ECC45j0oT72r.top"),sQuery(id+"F2.wireOp",EDGE,"CUWT8K6s-WbJc-WrEz-pjmn-ECC45j0oT72r.left"),sQuery(id+"F2.wireOp",EDGE,"CUWT8K6s-WbJc-WrEz-pjmn-ECC45j0oT72r.right")])]}),"instanceName":"21"});
            var Q66;
            Q66=makeQuery(id+"F4.opPattern","COPY",BODY,{"derivedFrom":makeQuery(id+"F3.opExtrude","SWEPT_BODY",BODY,{"disambiguationData":[OSD([sQuery(id+"F2.wireOp",EDGE,"E16.bottom"),sQuery(id+"F2.wireOp",EDGE,"E16.top"),sQuery(id+"F2.wireOp",EDGE,"E16.left"),sQuery(id+"F2.wireOp",EDGE,"E16.right")])]}),"instanceName":"22"});
            var Q67;
            Q67=makeQuery(id+"F4.opPattern","COPY",BODY,{"derivedFrom":makeQuery(id+"F3.opExtrude","SWEPT_BODY",BODY,{"disambiguationData":[OSD([sQuery(id+"F2.wireOp",EDGE,"E17.bottom"),sQuery(id+"F2.wireOp",EDGE,"E17.top"),sQuery(id+"F2.wireOp",EDGE,"E17.left"),sQuery(id+"F2.wireOp",EDGE,"E17.right")])]}),"instanceName":"22"});
            var Q68;
            Q68=makeQuery(id+"F4.opPattern","COPY",BODY,{"derivedFrom":makeQuery(id+"F3.opExtrude","SWEPT_BODY",BODY,{"disambiguationData":[OSD([sQuery(id+"F2.wireOp",EDGE,"CUWT8K6s-WbJc-WrEz-pjmn-ECC45j0oT72r.bottom"),sQuery(id+"F2.wireOp",EDGE,"CUWT8K6s-WbJc-WrEz-pjmn-ECC45j0oT72r.top"),sQuery(id+"F2.wireOp",EDGE,"CUWT8K6s-WbJc-WrEz-pjmn-ECC45j0oT72r.left"),sQuery(id+"F2.wireOp",EDGE,"CUWT8K6s-WbJc-WrEz-pjmn-ECC45j0oT72r.right")])]}),"instanceName":"22"});
            var Q69;
            Q69=makeQuery(id+"F4.opPattern","COPY",BODY,{"derivedFrom":makeQuery(id+"F3.opExtrude","SWEPT_BODY",BODY,{"disambiguationData":[OSD([sQuery(id+"F2.wireOp",EDGE,"E16.bottom"),sQuery(id+"F2.wireOp",EDGE,"E16.top"),sQuery(id+"F2.wireOp",EDGE,"E16.left"),sQuery(id+"F2.wireOp",EDGE,"E16.right")])]}),"instanceName":"23"});
            var Q70;
            Q70=makeQuery(id+"F4.opPattern","COPY",BODY,{"derivedFrom":makeQuery(id+"F3.opExtrude","SWEPT_BODY",BODY,{"disambiguationData":[OSD([sQuery(id+"F2.wireOp",EDGE,"E17.bottom"),sQuery(id+"F2.wireOp",EDGE,"E17.top"),sQuery(id+"F2.wireOp",EDGE,"E17.left"),sQuery(id+"F2.wireOp",EDGE,"E17.right")])]}),"instanceName":"23"});
            var Q71;
            Q71=makeQuery(id+"F4.opPattern","COPY",BODY,{"derivedFrom":makeQuery(id+"F3.opExtrude","SWEPT_BODY",BODY,{"disambiguationData":[OSD([sQuery(id+"F2.wireOp",EDGE,"CUWT8K6s-WbJc-WrEz-pjmn-ECC45j0oT72r.bottom"),sQuery(id+"F2.wireOp",EDGE,"CUWT8K6s-WbJc-WrEz-pjmn-ECC45j0oT72r.top"),sQuery(id+"F2.wireOp",EDGE,"CUWT8K6s-WbJc-WrEz-pjmn-ECC45j0oT72r.left"),sQuery(id+"F2.wireOp",EDGE,"CUWT8K6s-WbJc-WrEz-pjmn-ECC45j0oT72r.right")])]}),"instanceName":"23"});
            var Q72;
            Q72=makeQuery(id+"F4.opPattern","COPY",BODY,{"derivedFrom":makeQuery(id+"F3.opExtrude","SWEPT_BODY",BODY,{"disambiguationData":[OSD([sQuery(id+"F2.wireOp",EDGE,"E16.bottom"),sQuery(id+"F2.wireOp",EDGE,"E16.top"),sQuery(id+"F2.wireOp",EDGE,"E16.left"),sQuery(id+"F2.wireOp",EDGE,"E16.right")])]}),"instanceName":"24"});
            var Q73;
            Q73=makeQuery(id+"F4.opPattern","COPY",BODY,{"derivedFrom":makeQuery(id+"F3.opExtrude","SWEPT_BODY",BODY,{"disambiguationData":[OSD([sQuery(id+"F2.wireOp",EDGE,"E17.bottom"),sQuery(id+"F2.wireOp",EDGE,"E17.top"),sQuery(id+"F2.wireOp",EDGE,"E17.left"),sQuery(id+"F2.wireOp",EDGE,"E17.right")])]}),"instanceName":"24"});
            var Q74;
            Q74=makeQuery(id+"F4.opPattern","COPY",BODY,{"derivedFrom":makeQuery(id+"F3.opExtrude","SWEPT_BODY",BODY,{"disambiguationData":[OSD([sQuery(id+"F2.wireOp",EDGE,"CUWT8K6s-WbJc-WrEz-pjmn-ECC45j0oT72r.bottom"),sQuery(id+"F2.wireOp",EDGE,"CUWT8K6s-WbJc-WrEz-pjmn-ECC45j0oT72r.top"),sQuery(id+"F2.wireOp",EDGE,"CUWT8K6s-WbJc-WrEz-pjmn-ECC45j0oT72r.left"),sQuery(id+"F2.wireOp",EDGE,"CUWT8K6s-WbJc-WrEz-pjmn-ECC45j0oT72r.right")])]}),"instanceName":"24"});
            var Q75;
            Q75=makeQuery(id+"F4.opPattern","COPY",BODY,{"derivedFrom":makeQuery(id+"F3.opExtrude","SWEPT_BODY",BODY,{"disambiguationData":[OSD([sQuery(id+"F2.wireOp",EDGE,"E16.bottom"),sQuery(id+"F2.wireOp",EDGE,"E16.top"),sQuery(id+"F2.wireOp",EDGE,"E16.left"),sQuery(id+"F2.wireOp",EDGE,"E16.right")])]}),"instanceName":"25"});
            var Q76;
            Q76=makeQuery(id+"F4.opPattern","COPY",BODY,{"derivedFrom":makeQuery(id+"F3.opExtrude","SWEPT_BODY",BODY,{"disambiguationData":[OSD([sQuery(id+"F2.wireOp",EDGE,"E17.bottom"),sQuery(id+"F2.wireOp",EDGE,"E17.top"),sQuery(id+"F2.wireOp",EDGE,"E17.left"),sQuery(id+"F2.wireOp",EDGE,"E17.right")])]}),"instanceName":"25"});
            var Q77;
            Q77=makeQuery(id+"F4.opPattern","COPY",BODY,{"derivedFrom":makeQuery(id+"F3.opExtrude","SWEPT_BODY",BODY,{"disambiguationData":[OSD([sQuery(id+"F2.wireOp",EDGE,"CUWT8K6s-WbJc-WrEz-pjmn-ECC45j0oT72r.bottom"),sQuery(id+"F2.wireOp",EDGE,"CUWT8K6s-WbJc-WrEz-pjmn-ECC45j0oT72r.top"),sQuery(id+"F2.wireOp",EDGE,"CUWT8K6s-WbJc-WrEz-pjmn-ECC45j0oT72r.left"),sQuery(id+"F2.wireOp",EDGE,"CUWT8K6s-WbJc-WrEz-pjmn-ECC45j0oT72r.right")])]}),"instanceName":"25"});
            var Q78;
            Q78=makeQuery(id+"F4.opPattern","COPY",BODY,{"derivedFrom":makeQuery(id+"F3.opExtrude","SWEPT_BODY",BODY,{"disambiguationData":[OSD([sQuery(id+"F2.wireOp",EDGE,"E16.bottom"),sQuery(id+"F2.wireOp",EDGE,"E16.top"),sQuery(id+"F2.wireOp",EDGE,"E16.left"),sQuery(id+"F2.wireOp",EDGE,"E16.right")])]}),"instanceName":"26"});
            var Q79;
            Q79=makeQuery(id+"F4.opPattern","COPY",BODY,{"derivedFrom":makeQuery(id+"F3.opExtrude","SWEPT_BODY",BODY,{"disambiguationData":[OSD([sQuery(id+"F2.wireOp",EDGE,"E17.bottom"),sQuery(id+"F2.wireOp",EDGE,"E17.top"),sQuery(id+"F2.wireOp",EDGE,"E17.left"),sQuery(id+"F2.wireOp",EDGE,"E17.right")])]}),"instanceName":"26"});
            var Q80;
            Q80=makeQuery(id+"F4.opPattern","COPY",BODY,{"derivedFrom":makeQuery(id+"F3.opExtrude","SWEPT_BODY",BODY,{"disambiguationData":[OSD([sQuery(id+"F2.wireOp",EDGE,"CUWT8K6s-WbJc-WrEz-pjmn-ECC45j0oT72r.bottom"),sQuery(id+"F2.wireOp",EDGE,"CUWT8K6s-WbJc-WrEz-pjmn-ECC45j0oT72r.top"),sQuery(id+"F2.wireOp",EDGE,"CUWT8K6s-WbJc-WrEz-pjmn-ECC45j0oT72r.left"),sQuery(id+"F2.wireOp",EDGE,"CUWT8K6s-WbJc-WrEz-pjmn-ECC45j0oT72r.right")])]}),"instanceName":"26"});
            var Q81;
            Q81=makeQuery(id+"F4.opPattern","COPY",BODY,{"derivedFrom":makeQuery(id+"F3.opExtrude","SWEPT_BODY",BODY,{"disambiguationData":[OSD([sQuery(id+"F2.wireOp",EDGE,"E16.bottom"),sQuery(id+"F2.wireOp",EDGE,"E16.top"),sQuery(id+"F2.wireOp",EDGE,"E16.left"),sQuery(id+"F2.wireOp",EDGE,"E16.right")])]}),"instanceName":"27"});
            var Q82;
            Q82=makeQuery(id+"F4.opPattern","COPY",BODY,{"derivedFrom":makeQuery(id+"F3.opExtrude","SWEPT_BODY",BODY,{"disambiguationData":[OSD([sQuery(id+"F2.wireOp",EDGE,"E17.bottom"),sQuery(id+"F2.wireOp",EDGE,"E17.top"),sQuery(id+"F2.wireOp",EDGE,"E17.left"),sQuery(id+"F2.wireOp",EDGE,"E17.right")])]}),"instanceName":"27"});
            var Q83;
            Q83=makeQuery(id+"F4.opPattern","COPY",BODY,{"derivedFrom":makeQuery(id+"F3.opExtrude","SWEPT_BODY",BODY,{"disambiguationData":[OSD([sQuery(id+"F2.wireOp",EDGE,"CUWT8K6s-WbJc-WrEz-pjmn-ECC45j0oT72r.bottom"),sQuery(id+"F2.wireOp",EDGE,"CUWT8K6s-WbJc-WrEz-pjmn-ECC45j0oT72r.top"),sQuery(id+"F2.wireOp",EDGE,"CUWT8K6s-WbJc-WrEz-pjmn-ECC45j0oT72r.left"),sQuery(id+"F2.wireOp",EDGE,"CUWT8K6s-WbJc-WrEz-pjmn-ECC45j0oT72r.right")])]}),"instanceName":"27"});
            var Q84;
            Q84=makeQuery(id+"F4.opPattern","COPY",BODY,{"derivedFrom":makeQuery(id+"F3.opExtrude","SWEPT_BODY",BODY,{"disambiguationData":[OSD([sQuery(id+"F2.wireOp",EDGE,"E16.bottom"),sQuery(id+"F2.wireOp",EDGE,"E16.top"),sQuery(id+"F2.wireOp",EDGE,"E16.left"),sQuery(id+"F2.wireOp",EDGE,"E16.right")])]}),"instanceName":"28"});
            var Q85;
            Q85=makeQuery(id+"F4.opPattern","COPY",BODY,{"derivedFrom":makeQuery(id+"F3.opExtrude","SWEPT_BODY",BODY,{"disambiguationData":[OSD([sQuery(id+"F2.wireOp",EDGE,"E17.bottom"),sQuery(id+"F2.wireOp",EDGE,"E17.top"),sQuery(id+"F2.wireOp",EDGE,"E17.left"),sQuery(id+"F2.wireOp",EDGE,"E17.right")])]}),"instanceName":"28"});
            var Q86;
            Q86=makeQuery(id+"F4.opPattern","COPY",BODY,{"derivedFrom":makeQuery(id+"F3.opExtrude","SWEPT_BODY",BODY,{"disambiguationData":[OSD([sQuery(id+"F2.wireOp",EDGE,"CUWT8K6s-WbJc-WrEz-pjmn-ECC45j0oT72r.bottom"),sQuery(id+"F2.wireOp",EDGE,"CUWT8K6s-WbJc-WrEz-pjmn-ECC45j0oT72r.top"),sQuery(id+"F2.wireOp",EDGE,"CUWT8K6s-WbJc-WrEz-pjmn-ECC45j0oT72r.left"),sQuery(id+"F2.wireOp",EDGE,"CUWT8K6s-WbJc-WrEz-pjmn-ECC45j0oT72r.right")])]}),"instanceName":"28"});
            var Q87;
            Q87=makeQuery(id+"F4.opPattern","COPY",BODY,{"derivedFrom":makeQuery(id+"F3.opExtrude","SWEPT_BODY",BODY,{"disambiguationData":[OSD([sQuery(id+"F2.wireOp",EDGE,"E16.bottom"),sQuery(id+"F2.wireOp",EDGE,"E16.top"),sQuery(id+"F2.wireOp",EDGE,"E16.left"),sQuery(id+"F2.wireOp",EDGE,"E16.right")])]}),"instanceName":"29"});
            var Q88;
            Q88=makeQuery(id+"F4.opPattern","COPY",BODY,{"derivedFrom":makeQuery(id+"F3.opExtrude","SWEPT_BODY",BODY,{"disambiguationData":[OSD([sQuery(id+"F2.wireOp",EDGE,"E17.bottom"),sQuery(id+"F2.wireOp",EDGE,"E17.top"),sQuery(id+"F2.wireOp",EDGE,"E17.left"),sQuery(id+"F2.wireOp",EDGE,"E17.right")])]}),"instanceName":"29"});
            var Q89;
            Q89=makeQuery(id+"F4.opPattern","COPY",BODY,{"derivedFrom":makeQuery(id+"F3.opExtrude","SWEPT_BODY",BODY,{"disambiguationData":[OSD([sQuery(id+"F2.wireOp",EDGE,"CUWT8K6s-WbJc-WrEz-pjmn-ECC45j0oT72r.bottom"),sQuery(id+"F2.wireOp",EDGE,"CUWT8K6s-WbJc-WrEz-pjmn-ECC45j0oT72r.top"),sQuery(id+"F2.wireOp",EDGE,"CUWT8K6s-WbJc-WrEz-pjmn-ECC45j0oT72r.left"),sQuery(id+"F2.wireOp",EDGE,"CUWT8K6s-WbJc-WrEz-pjmn-ECC45j0oT72r.right")])]}),"instanceName":"29"});
            var Q90;
            Q90=makeQuery(id+"F4.opPattern","COPY",BODY,{"derivedFrom":makeQuery(id+"F3.opExtrude","SWEPT_BODY",BODY,{"disambiguationData":[OSD([sQuery(id+"F2.wireOp",EDGE,"E16.bottom"),sQuery(id+"F2.wireOp",EDGE,"E16.top"),sQuery(id+"F2.wireOp",EDGE,"E16.left"),sQuery(id+"F2.wireOp",EDGE,"E16.right")])]}),"instanceName":"30"});
            var Q91;
            Q91=makeQuery(id+"F4.opPattern","COPY",BODY,{"derivedFrom":makeQuery(id+"F3.opExtrude","SWEPT_BODY",BODY,{"disambiguationData":[OSD([sQuery(id+"F2.wireOp",EDGE,"E17.bottom"),sQuery(id+"F2.wireOp",EDGE,"E17.top"),sQuery(id+"F2.wireOp",EDGE,"E17.left"),sQuery(id+"F2.wireOp",EDGE,"E17.right")])]}),"instanceName":"30"});
            var Q92;
            Q92=makeQuery(id+"F4.opPattern","COPY",BODY,{"derivedFrom":makeQuery(id+"F3.opExtrude","SWEPT_BODY",BODY,{"disambiguationData":[OSD([sQuery(id+"F2.wireOp",EDGE,"CUWT8K6s-WbJc-WrEz-pjmn-ECC45j0oT72r.bottom"),sQuery(id+"F2.wireOp",EDGE,"CUWT8K6s-WbJc-WrEz-pjmn-ECC45j0oT72r.top"),sQuery(id+"F2.wireOp",EDGE,"CUWT8K6s-WbJc-WrEz-pjmn-ECC45j0oT72r.left"),sQuery(id+"F2.wireOp",EDGE,"CUWT8K6s-WbJc-WrEz-pjmn-ECC45j0oT72r.right")])]}),"instanceName":"30"});
            var Q93;
            Q93=makeQuery(id+"F4.opPattern","COPY",BODY,{"derivedFrom":makeQuery(id+"F3.opExtrude","SWEPT_BODY",BODY,{"disambiguationData":[OSD([sQuery(id+"F2.wireOp",EDGE,"E16.bottom"),sQuery(id+"F2.wireOp",EDGE,"E16.top"),sQuery(id+"F2.wireOp",EDGE,"E16.left"),sQuery(id+"F2.wireOp",EDGE,"E16.right")])]}),"instanceName":"31"});
            var Q94;
            Q94=makeQuery(id+"F4.opPattern","COPY",BODY,{"derivedFrom":makeQuery(id+"F3.opExtrude","SWEPT_BODY",BODY,{"disambiguationData":[OSD([sQuery(id+"F2.wireOp",EDGE,"E17.bottom"),sQuery(id+"F2.wireOp",EDGE,"E17.top"),sQuery(id+"F2.wireOp",EDGE,"E17.left"),sQuery(id+"F2.wireOp",EDGE,"E17.right")])]}),"instanceName":"31"});
            var Q95;
            Q95=makeQuery(id+"F4.opPattern","COPY",BODY,{"derivedFrom":makeQuery(id+"F3.opExtrude","SWEPT_BODY",BODY,{"disambiguationData":[OSD([sQuery(id+"F2.wireOp",EDGE,"CUWT8K6s-WbJc-WrEz-pjmn-ECC45j0oT72r.bottom"),sQuery(id+"F2.wireOp",EDGE,"CUWT8K6s-WbJc-WrEz-pjmn-ECC45j0oT72r.top"),sQuery(id+"F2.wireOp",EDGE,"CUWT8K6s-WbJc-WrEz-pjmn-ECC45j0oT72r.left"),sQuery(id+"F2.wireOp",EDGE,"CUWT8K6s-WbJc-WrEz-pjmn-ECC45j0oT72r.right")])]}),"instanceName":"31"});
            var Q96;
            Q96=makeQuery(id+"F4.opPattern","COPY",BODY,{"derivedFrom":makeQuery(id+"F3.opExtrude","SWEPT_BODY",BODY,{"disambiguationData":[OSD([sQuery(id+"F2.wireOp",EDGE,"E16.bottom"),sQuery(id+"F2.wireOp",EDGE,"E16.top"),sQuery(id+"F2.wireOp",EDGE,"E16.left"),sQuery(id+"F2.wireOp",EDGE,"E16.right")])]}),"instanceName":"32"});
            var Q97;
            Q97=makeQuery(id+"F4.opPattern","COPY",BODY,{"derivedFrom":makeQuery(id+"F3.opExtrude","SWEPT_BODY",BODY,{"disambiguationData":[OSD([sQuery(id+"F2.wireOp",EDGE,"E17.bottom"),sQuery(id+"F2.wireOp",EDGE,"E17.top"),sQuery(id+"F2.wireOp",EDGE,"E17.left"),sQuery(id+"F2.wireOp",EDGE,"E17.right")])]}),"instanceName":"32"});
            var Q98;
            Q98=makeQuery(id+"F4.opPattern","COPY",BODY,{"derivedFrom":makeQuery(id+"F3.opExtrude","SWEPT_BODY",BODY,{"disambiguationData":[OSD([sQuery(id+"F2.wireOp",EDGE,"CUWT8K6s-WbJc-WrEz-pjmn-ECC45j0oT72r.bottom"),sQuery(id+"F2.wireOp",EDGE,"CUWT8K6s-WbJc-WrEz-pjmn-ECC45j0oT72r.top"),sQuery(id+"F2.wireOp",EDGE,"CUWT8K6s-WbJc-WrEz-pjmn-ECC45j0oT72r.left"),sQuery(id+"F2.wireOp",EDGE,"CUWT8K6s-WbJc-WrEz-pjmn-ECC45j0oT72r.right")])]}),"instanceName":"32"});
            var Q99;
            Q99=makeQuery(id+"F4.opPattern","COPY",BODY,{"derivedFrom":makeQuery(id+"F3.opExtrude","SWEPT_BODY",BODY,{"disambiguationData":[OSD([sQuery(id+"F2.wireOp",EDGE,"E16.bottom"),sQuery(id+"F2.wireOp",EDGE,"E16.top"),sQuery(id+"F2.wireOp",EDGE,"E16.left"),sQuery(id+"F2.wireOp",EDGE,"E16.right")])]}),"instanceName":"33"});
            var Q100;
            Q100=makeQuery(id+"F4.opPattern","COPY",BODY,{"derivedFrom":makeQuery(id+"F3.opExtrude","SWEPT_BODY",BODY,{"disambiguationData":[OSD([sQuery(id+"F2.wireOp",EDGE,"E17.bottom"),sQuery(id+"F2.wireOp",EDGE,"E17.top"),sQuery(id+"F2.wireOp",EDGE,"E17.left"),sQuery(id+"F2.wireOp",EDGE,"E17.right")])]}),"instanceName":"33"});
            var Q101;
            Q101=makeQuery(id+"F4.opPattern","COPY",BODY,{"derivedFrom":makeQuery(id+"F3.opExtrude","SWEPT_BODY",BODY,{"disambiguationData":[OSD([sQuery(id+"F2.wireOp",EDGE,"CUWT8K6s-WbJc-WrEz-pjmn-ECC45j0oT72r.bottom"),sQuery(id+"F2.wireOp",EDGE,"CUWT8K6s-WbJc-WrEz-pjmn-ECC45j0oT72r.top"),sQuery(id+"F2.wireOp",EDGE,"CUWT8K6s-WbJc-WrEz-pjmn-ECC45j0oT72r.left"),sQuery(id+"F2.wireOp",EDGE,"CUWT8K6s-WbJc-WrEz-pjmn-ECC45j0oT72r.right")])]}),"instanceName":"33"});
            var Q102;
            Q102=makeQuery(id+"F4.opPattern","COPY",BODY,{"derivedFrom":makeQuery(id+"F3.opExtrude","SWEPT_BODY",BODY,{"disambiguationData":[OSD([sQuery(id+"F2.wireOp",EDGE,"E16.bottom"),sQuery(id+"F2.wireOp",EDGE,"E16.top"),sQuery(id+"F2.wireOp",EDGE,"E16.left"),sQuery(id+"F2.wireOp",EDGE,"E16.right")])]}),"instanceName":"34"});
            var Q103;
            Q103=makeQuery(id+"F4.opPattern","COPY",BODY,{"derivedFrom":makeQuery(id+"F3.opExtrude","SWEPT_BODY",BODY,{"disambiguationData":[OSD([sQuery(id+"F2.wireOp",EDGE,"E17.bottom"),sQuery(id+"F2.wireOp",EDGE,"E17.top"),sQuery(id+"F2.wireOp",EDGE,"E17.left"),sQuery(id+"F2.wireOp",EDGE,"E17.right")])]}),"instanceName":"34"});
            var Q104;
            Q104=makeQuery(id+"F4.opPattern","COPY",BODY,{"derivedFrom":makeQuery(id+"F3.opExtrude","SWEPT_BODY",BODY,{"disambiguationData":[OSD([sQuery(id+"F2.wireOp",EDGE,"CUWT8K6s-WbJc-WrEz-pjmn-ECC45j0oT72r.bottom"),sQuery(id+"F2.wireOp",EDGE,"CUWT8K6s-WbJc-WrEz-pjmn-ECC45j0oT72r.top"),sQuery(id+"F2.wireOp",EDGE,"CUWT8K6s-WbJc-WrEz-pjmn-ECC45j0oT72r.left"),sQuery(id+"F2.wireOp",EDGE,"CUWT8K6s-WbJc-WrEz-pjmn-ECC45j0oT72r.right")])]}),"instanceName":"34"});
            var Q105;
            Q105=makeQuery(id+"F4.opPattern","COPY",BODY,{"derivedFrom":makeQuery(id+"F3.opExtrude","SWEPT_BODY",BODY,{"disambiguationData":[OSD([sQuery(id+"F2.wireOp",EDGE,"E16.bottom"),sQuery(id+"F2.wireOp",EDGE,"E16.top"),sQuery(id+"F2.wireOp",EDGE,"E16.left"),sQuery(id+"F2.wireOp",EDGE,"E16.right")])]}),"instanceName":"35"});
            var Q106;
            Q106=makeQuery(id+"F4.opPattern","COPY",BODY,{"derivedFrom":makeQuery(id+"F3.opExtrude","SWEPT_BODY",BODY,{"disambiguationData":[OSD([sQuery(id+"F2.wireOp",EDGE,"E17.bottom"),sQuery(id+"F2.wireOp",EDGE,"E17.top"),sQuery(id+"F2.wireOp",EDGE,"E17.left"),sQuery(id+"F2.wireOp",EDGE,"E17.right")])]}),"instanceName":"35"});
            var Q107;
            Q107=makeQuery(id+"F4.opPattern","COPY",BODY,{"derivedFrom":makeQuery(id+"F3.opExtrude","SWEPT_BODY",BODY,{"disambiguationData":[OSD([sQuery(id+"F2.wireOp",EDGE,"CUWT8K6s-WbJc-WrEz-pjmn-ECC45j0oT72r.bottom"),sQuery(id+"F2.wireOp",EDGE,"CUWT8K6s-WbJc-WrEz-pjmn-ECC45j0oT72r.top"),sQuery(id+"F2.wireOp",EDGE,"CUWT8K6s-WbJc-WrEz-pjmn-ECC45j0oT72r.left"),sQuery(id+"F2.wireOp",EDGE,"CUWT8K6s-WbJc-WrEz-pjmn-ECC45j0oT72r.right")])]}),"instanceName":"35"});
            var Q108;
            Q108=makeQuery(id+"F4.opPattern","COPY",BODY,{"derivedFrom":makeQuery(id+"F3.opExtrude","SWEPT_BODY",BODY,{"disambiguationData":[OSD([sQuery(id+"F2.wireOp",EDGE,"E16.bottom"),sQuery(id+"F2.wireOp",EDGE,"E16.top"),sQuery(id+"F2.wireOp",EDGE,"E16.left"),sQuery(id+"F2.wireOp",EDGE,"E16.right")])]}),"instanceName":"36"});
            var Q109;
            Q109=makeQuery(id+"F4.opPattern","COPY",BODY,{"derivedFrom":makeQuery(id+"F3.opExtrude","SWEPT_BODY",BODY,{"disambiguationData":[OSD([sQuery(id+"F2.wireOp",EDGE,"E17.bottom"),sQuery(id+"F2.wireOp",EDGE,"E17.top"),sQuery(id+"F2.wireOp",EDGE,"E17.left"),sQuery(id+"F2.wireOp",EDGE,"E17.right")])]}),"instanceName":"36"});
            var Q110;
            Q110=makeQuery(id+"F4.opPattern","COPY",BODY,{"derivedFrom":makeQuery(id+"F3.opExtrude","SWEPT_BODY",BODY,{"disambiguationData":[OSD([sQuery(id+"F2.wireOp",EDGE,"CUWT8K6s-WbJc-WrEz-pjmn-ECC45j0oT72r.bottom"),sQuery(id+"F2.wireOp",EDGE,"CUWT8K6s-WbJc-WrEz-pjmn-ECC45j0oT72r.top"),sQuery(id+"F2.wireOp",EDGE,"CUWT8K6s-WbJc-WrEz-pjmn-ECC45j0oT72r.left"),sQuery(id+"F2.wireOp",EDGE,"CUWT8K6s-WbJc-WrEz-pjmn-ECC45j0oT72r.right")])]}),"instanceName":"36"});
            var Q111;
            Q111=makeQuery(id+"F4.opPattern","COPY",BODY,{"derivedFrom":makeQuery(id+"F3.opExtrude","SWEPT_BODY",BODY,{"disambiguationData":[OSD([sQuery(id+"F2.wireOp",EDGE,"E16.bottom"),sQuery(id+"F2.wireOp",EDGE,"E16.top"),sQuery(id+"F2.wireOp",EDGE,"E16.left"),sQuery(id+"F2.wireOp",EDGE,"E16.right")])]}),"instanceName":"37"});
            var Q112;
            Q112=makeQuery(id+"F4.opPattern","COPY",BODY,{"derivedFrom":makeQuery(id+"F3.opExtrude","SWEPT_BODY",BODY,{"disambiguationData":[OSD([sQuery(id+"F2.wireOp",EDGE,"E17.bottom"),sQuery(id+"F2.wireOp",EDGE,"E17.top"),sQuery(id+"F2.wireOp",EDGE,"E17.left"),sQuery(id+"F2.wireOp",EDGE,"E17.right")])]}),"instanceName":"37"});
            var Q113;
            Q113=makeQuery(id+"F4.opPattern","COPY",BODY,{"derivedFrom":makeQuery(id+"F3.opExtrude","SWEPT_BODY",BODY,{"disambiguationData":[OSD([sQuery(id+"F2.wireOp",EDGE,"CUWT8K6s-WbJc-WrEz-pjmn-ECC45j0oT72r.bottom"),sQuery(id+"F2.wireOp",EDGE,"CUWT8K6s-WbJc-WrEz-pjmn-ECC45j0oT72r.top"),sQuery(id+"F2.wireOp",EDGE,"CUWT8K6s-WbJc-WrEz-pjmn-ECC45j0oT72r.left"),sQuery(id+"F2.wireOp",EDGE,"CUWT8K6s-WbJc-WrEz-pjmn-ECC45j0oT72r.right")])]}),"instanceName":"37"});
            var Q114;
            Q114=makeQuery(id+"F4.opPattern","COPY",BODY,{"derivedFrom":makeQuery(id+"F3.opExtrude","SWEPT_BODY",BODY,{"disambiguationData":[OSD([sQuery(id+"F2.wireOp",EDGE,"E16.bottom"),sQuery(id+"F2.wireOp",EDGE,"E16.top"),sQuery(id+"F2.wireOp",EDGE,"E16.left"),sQuery(id+"F2.wireOp",EDGE,"E16.right")])]}),"instanceName":"38"});
            var Q115;
            Q115=makeQuery(id+"F4.opPattern","COPY",BODY,{"derivedFrom":makeQuery(id+"F3.opExtrude","SWEPT_BODY",BODY,{"disambiguationData":[OSD([sQuery(id+"F2.wireOp",EDGE,"E17.bottom"),sQuery(id+"F2.wireOp",EDGE,"E17.top"),sQuery(id+"F2.wireOp",EDGE,"E17.left"),sQuery(id+"F2.wireOp",EDGE,"E17.right")])]}),"instanceName":"38"});
            var Q116;
            Q116=makeQuery(id+"F4.opPattern","COPY",BODY,{"derivedFrom":makeQuery(id+"F3.opExtrude","SWEPT_BODY",BODY,{"disambiguationData":[OSD([sQuery(id+"F2.wireOp",EDGE,"CUWT8K6s-WbJc-WrEz-pjmn-ECC45j0oT72r.bottom"),sQuery(id+"F2.wireOp",EDGE,"CUWT8K6s-WbJc-WrEz-pjmn-ECC45j0oT72r.top"),sQuery(id+"F2.wireOp",EDGE,"CUWT8K6s-WbJc-WrEz-pjmn-ECC45j0oT72r.left"),sQuery(id+"F2.wireOp",EDGE,"CUWT8K6s-WbJc-WrEz-pjmn-ECC45j0oT72r.right")])]}),"instanceName":"38"});
            var Q117;
            Q117=makeQuery(id+"F4.opPattern","COPY",BODY,{"derivedFrom":makeQuery(id+"F3.opExtrude","SWEPT_BODY",BODY,{"disambiguationData":[OSD([sQuery(id+"F2.wireOp",EDGE,"E16.bottom"),sQuery(id+"F2.wireOp",EDGE,"E16.top"),sQuery(id+"F2.wireOp",EDGE,"E16.left"),sQuery(id+"F2.wireOp",EDGE,"E16.right")])]}),"instanceName":"39"});
            var Q118;
            Q118=makeQuery(id+"F4.opPattern","COPY",BODY,{"derivedFrom":makeQuery(id+"F3.opExtrude","SWEPT_BODY",BODY,{"disambiguationData":[OSD([sQuery(id+"F2.wireOp",EDGE,"E17.bottom"),sQuery(id+"F2.wireOp",EDGE,"E17.top"),sQuery(id+"F2.wireOp",EDGE,"E17.left"),sQuery(id+"F2.wireOp",EDGE,"E17.right")])]}),"instanceName":"39"});
            var Q119;
            Q119=makeQuery(id+"F4.opPattern","COPY",BODY,{"derivedFrom":makeQuery(id+"F3.opExtrude","SWEPT_BODY",BODY,{"disambiguationData":[OSD([sQuery(id+"F2.wireOp",EDGE,"CUWT8K6s-WbJc-WrEz-pjmn-ECC45j0oT72r.bottom"),sQuery(id+"F2.wireOp",EDGE,"CUWT8K6s-WbJc-WrEz-pjmn-ECC45j0oT72r.top"),sQuery(id+"F2.wireOp",EDGE,"CUWT8K6s-WbJc-WrEz-pjmn-ECC45j0oT72r.left"),sQuery(id+"F2.wireOp",EDGE,"CUWT8K6s-WbJc-WrEz-pjmn-ECC45j0oT72r.right")])]}),"instanceName":"39"});
            var Q120;
            Q120=makeQuery(id+"F1.opRevolve","SWEPT_BODY",BODY,{"disambiguationData":[OSD([sQuery(id+"F0.wireOp",EDGE,"E1"),sQuery(id+"F0.wireOp",EDGE,"E2"),sQuery(id+"F0.wireOp",EDGE,"E3"),sQuery(id+"F0.wireOp",EDGE,"E4"),sQuery(id+"F0.wireOp",EDGE,"E5.filletArc"),sQuery(id+"F0.wireOp",EDGE,"E6.filletArc"),sQuery(id+"F0.wireOp",EDGE,"E7"),sQuery(id+"F0.wireOp",EDGE,"E9.0"),sQuery(id+"F0.wireOp",EDGE,"E9.1"),sQuery(id+"F0.wireOp",EDGE,"E9.2"),sQuery(id+"F0.wireOp",EDGE,"E9.3"),sQuery(id+"F0.wireOp",EDGE,"E9.4"),sQuery(id+"F0.wireOp",EDGE,"E9.5"),sQuery(id+"F0.wireOp",EDGE,"E10"),sQuery(id+"F0.wireOp",EDGE,"E11"),sQuery(id+"F0.wireOp",EDGE,"E12")])]});
            booleanBodies(context, id + "F5", {"operationType" : BooleanOperationType.SUBTRACTION, "tools" : qUnion([Q0, Q1, Q2, Q3, Q4, Q5, Q6, Q7, Q8, Q9, Q10, Q11, Q12, Q13, Q14, Q15, Q16, Q17, Q18, Q19, Q20, Q21, Q22, Q23, Q24, Q25, Q26, Q27, Q28, Q29, Q30, Q31, Q32, Q33, Q34, Q35, Q36, Q37, Q38, Q39, Q40, Q41, Q42, Q43, Q44, Q45, Q46, Q47, Q48, Q49, Q50, Q51, Q52, Q53, Q54, Q55, Q56, Q57, Q58, Q59, Q60, Q61, Q62, Q63, Q64, Q65, Q66, Q67, Q68, Q69, Q70, Q71, Q72, Q73, Q74, Q75, Q76, Q77, Q78, Q79, Q80, Q81, Q82, Q83, Q84, Q85, Q86, Q87, Q88, Q89, Q90, Q91, Q92, Q93, Q94, Q95, Q96, Q97, Q98, Q99, Q100, Q101, Q102, Q103, Q104, Q105, Q106, Q107, Q108, Q109, Q110, Q111, Q112, Q113, Q114, Q115, Q116, Q117, Q118, Q119]), "targets" : qUnion([Q120])});
        }
        {
            var Q0;
            Q0=qCreatedBy(makeId("Front.planeOp"),FACE);
            var sketch = newSketch(context, id + "F6", { "sketchPlane" : qUnion([Q0])});
            skLineSegment(sketch, "E18", {"start": v(0, 0) * mm, "end": v(0, 69.5) * mm, "construction": true});
            skLineSegment(sketch, "E19.bottom", {"start": v(0.75, 63.5) * mm, "end": v(-0.75, 63.5) * mm});
            skLineSegment(sketch, "E19.top", {"start": v(0.75, 75.5) * mm, "end": v(-0.75, 75.5) * mm});
            skLineSegment(sketch, "E19.left", {"start": v(0.75, 63.5) * mm, "end": v(0.75, 75.5) * mm});
            skLineSegment(sketch, "E19.right", {"start": v(-0.75, 63.5) * mm, "end": v(-0.75, 75.5) * mm});
            skPoint(sketch, "E19.middle", {"position": v(0, 69.5) * mm});
            skSolve(sketch);
        }
        {
            var Q0;
            Q0 = qSketchRegion(id + "F6", true);
            extrude(context, id + "F7", {"entities" : qUnion([Q0]), "depth" : 30 * mm, "offsetDistance" : 25 * mm});
        }
        {
            var Q0;
            Q0=makeQuery(id+"F7.opExtrude","SWEPT_BODY",BODY,{"disambiguationData":[OSD([sQuery(id+"F6.wireOp",EDGE,"E19.bottom"),sQuery(id+"F6.wireOp",EDGE,"E19.top"),sQuery(id+"F6.wireOp",EDGE,"E19.left"),sQuery(id+"F6.wireOp",EDGE,"E19.right")])]});
            var Q1;
            Q1=sQuery(id+"F0.wireOp",EDGE,"E0");
            circularPattern(context, id + "F8", {"entities" : qUnion([Q0]), "axis" : qUnion([Q1]), "angle" : 360 * degree, "instanceCount" : 15, "equalSpace" : true});
        }
        {
            var Q0;
            Q0=makeQuery(id+"F7.opExtrude","SWEPT_BODY",BODY,{"disambiguationData":[OSD([sQuery(id+"F6.wireOp",EDGE,"E19.bottom"),sQuery(id+"F6.wireOp",EDGE,"E19.top"),sQuery(id+"F6.wireOp",EDGE,"E19.left"),sQuery(id+"F6.wireOp",EDGE,"E19.right")])]});
            var Q1;
            Q1=makeQuery(id+"F8.opPattern","COPY",BODY,{"derivedFrom":makeQuery(id+"F7.opExtrude","SWEPT_BODY",BODY,{"disambiguationData":[OSD([sQuery(id+"F6.wireOp",EDGE,"E19.bottom"),sQuery(id+"F6.wireOp",EDGE,"E19.top"),sQuery(id+"F6.wireOp",EDGE,"E19.left"),sQuery(id+"F6.wireOp",EDGE,"E19.right")])]}),"instanceName":"1"});
            var Q2;
            Q2=makeQuery(id+"F8.opPattern","COPY",BODY,{"derivedFrom":makeQuery(id+"F7.opExtrude","SWEPT_BODY",BODY,{"disambiguationData":[OSD([sQuery(id+"F6.wireOp",EDGE,"E19.bottom"),sQuery(id+"F6.wireOp",EDGE,"E19.top"),sQuery(id+"F6.wireOp",EDGE,"E19.left"),sQuery(id+"F6.wireOp",EDGE,"E19.right")])]}),"instanceName":"2"});
            var Q3;
            Q3=makeQuery(id+"F8.opPattern","COPY",BODY,{"derivedFrom":makeQuery(id+"F7.opExtrude","SWEPT_BODY",BODY,{"disambiguationData":[OSD([sQuery(id+"F6.wireOp",EDGE,"E19.bottom"),sQuery(id+"F6.wireOp",EDGE,"E19.top"),sQuery(id+"F6.wireOp",EDGE,"E19.left"),sQuery(id+"F6.wireOp",EDGE,"E19.right")])]}),"instanceName":"3"});
            var Q4;
            Q4=makeQuery(id+"F8.opPattern","COPY",BODY,{"derivedFrom":makeQuery(id+"F7.opExtrude","SWEPT_BODY",BODY,{"disambiguationData":[OSD([sQuery(id+"F6.wireOp",EDGE,"E19.bottom"),sQuery(id+"F6.wireOp",EDGE,"E19.top"),sQuery(id+"F6.wireOp",EDGE,"E19.left"),sQuery(id+"F6.wireOp",EDGE,"E19.right")])]}),"instanceName":"4"});
            var Q5;
            Q5=makeQuery(id+"F8.opPattern","COPY",BODY,{"derivedFrom":makeQuery(id+"F7.opExtrude","SWEPT_BODY",BODY,{"disambiguationData":[OSD([sQuery(id+"F6.wireOp",EDGE,"E19.bottom"),sQuery(id+"F6.wireOp",EDGE,"E19.top"),sQuery(id+"F6.wireOp",EDGE,"E19.left"),sQuery(id+"F6.wireOp",EDGE,"E19.right")])]}),"instanceName":"5"});
            var Q6;
            Q6=makeQuery(id+"F8.opPattern","COPY",BODY,{"derivedFrom":makeQuery(id+"F7.opExtrude","SWEPT_BODY",BODY,{"disambiguationData":[OSD([sQuery(id+"F6.wireOp",EDGE,"E19.bottom"),sQuery(id+"F6.wireOp",EDGE,"E19.top"),sQuery(id+"F6.wireOp",EDGE,"E19.left"),sQuery(id+"F6.wireOp",EDGE,"E19.right")])]}),"instanceName":"6"});
            var Q7;
            Q7=makeQuery(id+"F8.opPattern","COPY",BODY,{"derivedFrom":makeQuery(id+"F7.opExtrude","SWEPT_BODY",BODY,{"disambiguationData":[OSD([sQuery(id+"F6.wireOp",EDGE,"E19.bottom"),sQuery(id+"F6.wireOp",EDGE,"E19.top"),sQuery(id+"F6.wireOp",EDGE,"E19.left"),sQuery(id+"F6.wireOp",EDGE,"E19.right")])]}),"instanceName":"7"});
            var Q8;
            Q8=makeQuery(id+"F8.opPattern","COPY",BODY,{"derivedFrom":makeQuery(id+"F7.opExtrude","SWEPT_BODY",BODY,{"disambiguationData":[OSD([sQuery(id+"F6.wireOp",EDGE,"E19.bottom"),sQuery(id+"F6.wireOp",EDGE,"E19.top"),sQuery(id+"F6.wireOp",EDGE,"E19.left"),sQuery(id+"F6.wireOp",EDGE,"E19.right")])]}),"instanceName":"8"});
            var Q9;
            Q9=makeQuery(id+"F8.opPattern","COPY",BODY,{"derivedFrom":makeQuery(id+"F7.opExtrude","SWEPT_BODY",BODY,{"disambiguationData":[OSD([sQuery(id+"F6.wireOp",EDGE,"E19.bottom"),sQuery(id+"F6.wireOp",EDGE,"E19.top"),sQuery(id+"F6.wireOp",EDGE,"E19.left"),sQuery(id+"F6.wireOp",EDGE,"E19.right")])]}),"instanceName":"9"});
            var Q10;
            Q10=makeQuery(id+"F8.opPattern","COPY",BODY,{"derivedFrom":makeQuery(id+"F7.opExtrude","SWEPT_BODY",BODY,{"disambiguationData":[OSD([sQuery(id+"F6.wireOp",EDGE,"E19.bottom"),sQuery(id+"F6.wireOp",EDGE,"E19.top"),sQuery(id+"F6.wireOp",EDGE,"E19.left"),sQuery(id+"F6.wireOp",EDGE,"E19.right")])]}),"instanceName":"10"});
            var Q11;
            Q11=makeQuery(id+"F8.opPattern","COPY",BODY,{"derivedFrom":makeQuery(id+"F7.opExtrude","SWEPT_BODY",BODY,{"disambiguationData":[OSD([sQuery(id+"F6.wireOp",EDGE,"E19.bottom"),sQuery(id+"F6.wireOp",EDGE,"E19.top"),sQuery(id+"F6.wireOp",EDGE,"E19.left"),sQuery(id+"F6.wireOp",EDGE,"E19.right")])]}),"instanceName":"11"});
            var Q12;
            Q12=makeQuery(id+"F8.opPattern","COPY",BODY,{"derivedFrom":makeQuery(id+"F7.opExtrude","SWEPT_BODY",BODY,{"disambiguationData":[OSD([sQuery(id+"F6.wireOp",EDGE,"E19.bottom"),sQuery(id+"F6.wireOp",EDGE,"E19.top"),sQuery(id+"F6.wireOp",EDGE,"E19.left"),sQuery(id+"F6.wireOp",EDGE,"E19.right")])]}),"instanceName":"12"});
            var Q13;
            Q13=makeQuery(id+"F8.opPattern","COPY",BODY,{"derivedFrom":makeQuery(id+"F7.opExtrude","SWEPT_BODY",BODY,{"disambiguationData":[OSD([sQuery(id+"F6.wireOp",EDGE,"E19.bottom"),sQuery(id+"F6.wireOp",EDGE,"E19.top"),sQuery(id+"F6.wireOp",EDGE,"E19.left"),sQuery(id+"F6.wireOp",EDGE,"E19.right")])]}),"instanceName":"13"});
            var Q14;
            Q14=makeQuery(id+"F8.opPattern","COPY",BODY,{"derivedFrom":makeQuery(id+"F7.opExtrude","SWEPT_BODY",BODY,{"disambiguationData":[OSD([sQuery(id+"F6.wireOp",EDGE,"E19.bottom"),sQuery(id+"F6.wireOp",EDGE,"E19.top"),sQuery(id+"F6.wireOp",EDGE,"E19.left"),sQuery(id+"F6.wireOp",EDGE,"E19.right")])]}),"instanceName":"14"});
            var Q15;
            Q15=makeQuery(id+"F8.opPattern","COPY",BODY,{"derivedFrom":makeQuery(id+"F7.opExtrude","SWEPT_BODY",BODY,{"disambiguationData":[OSD([sQuery(id+"F6.wireOp",EDGE,"E19.bottom"),sQuery(id+"F6.wireOp",EDGE,"E19.top"),sQuery(id+"F6.wireOp",EDGE,"E19.left"),sQuery(id+"F6.wireOp",EDGE,"E19.right")])]}),"instanceName":"15"});
            var Q16;
            Q16=makeQuery(id+"F8.opPattern","COPY",BODY,{"derivedFrom":makeQuery(id+"F7.opExtrude","SWEPT_BODY",BODY,{"disambiguationData":[OSD([sQuery(id+"F6.wireOp",EDGE,"E19.bottom"),sQuery(id+"F6.wireOp",EDGE,"E19.top"),sQuery(id+"F6.wireOp",EDGE,"E19.left"),sQuery(id+"F6.wireOp",EDGE,"E19.right")])]}),"instanceName":"16"});
            var Q17;
            Q17=makeQuery(id+"F8.opPattern","COPY",BODY,{"derivedFrom":makeQuery(id+"F7.opExtrude","SWEPT_BODY",BODY,{"disambiguationData":[OSD([sQuery(id+"F6.wireOp",EDGE,"E19.bottom"),sQuery(id+"F6.wireOp",EDGE,"E19.top"),sQuery(id+"F6.wireOp",EDGE,"E19.left"),sQuery(id+"F6.wireOp",EDGE,"E19.right")])]}),"instanceName":"17"});
            var Q18;
            Q18=makeQuery(id+"F8.opPattern","COPY",BODY,{"derivedFrom":makeQuery(id+"F7.opExtrude","SWEPT_BODY",BODY,{"disambiguationData":[OSD([sQuery(id+"F6.wireOp",EDGE,"E19.bottom"),sQuery(id+"F6.wireOp",EDGE,"E19.top"),sQuery(id+"F6.wireOp",EDGE,"E19.left"),sQuery(id+"F6.wireOp",EDGE,"E19.right")])]}),"instanceName":"18"});
            var Q19;
            Q19=makeQuery(id+"F8.opPattern","COPY",BODY,{"derivedFrom":makeQuery(id+"F7.opExtrude","SWEPT_BODY",BODY,{"disambiguationData":[OSD([sQuery(id+"F6.wireOp",EDGE,"E19.bottom"),sQuery(id+"F6.wireOp",EDGE,"E19.top"),sQuery(id+"F6.wireOp",EDGE,"E19.left"),sQuery(id+"F6.wireOp",EDGE,"E19.right")])]}),"instanceName":"19"});
            var Q20;
            Q20=makeQuery(id+"F1.opRevolve","SWEPT_BODY",BODY,{"disambiguationData":[OSD([sQuery(id+"F0.wireOp",EDGE,"E1"),sQuery(id+"F0.wireOp",EDGE,"E2"),sQuery(id+"F0.wireOp",EDGE,"E3"),sQuery(id+"F0.wireOp",EDGE,"E4"),sQuery(id+"F0.wireOp",EDGE,"E5.filletArc"),sQuery(id+"F0.wireOp",EDGE,"E6.filletArc"),sQuery(id+"F0.wireOp",EDGE,"E7"),sQuery(id+"F0.wireOp",EDGE,"E9.0"),sQuery(id+"F0.wireOp",EDGE,"E9.1"),sQuery(id+"F0.wireOp",EDGE,"E9.2"),sQuery(id+"F0.wireOp",EDGE,"E9.3"),sQuery(id+"F0.wireOp",EDGE,"E9.4"),sQuery(id+"F0.wireOp",EDGE,"E9.5"),sQuery(id+"F0.wireOp",EDGE,"E10"),sQuery(id+"F0.wireOp",EDGE,"E11"),sQuery(id+"F0.wireOp",EDGE,"E12")])]});
            booleanBodies(context, id + "F9", {"operationType" : BooleanOperationType.SUBTRACTION, "tools" : qUnion([Q0, Q1, Q2, Q3, Q4, Q5, Q6, Q7, Q8, Q9, Q10, Q11, Q12, Q13, Q14, Q15, Q16, Q17, Q18, Q19]), "targets" : qUnion([Q20])});
        }
        {
            var Q0;
            Q0=makeQuery(id+"F1.opRevolve","SWEPT_FACE",FACE,{"disambiguationData":[OSD([sQuery(id+"F0.wireOp",EDGE,"E1")])]});
            var sketch = newSketch(context, id + "F10", { "sketchPlane" : qUnion([Q0])});
            skArc(sketch, "E20", {"start": v(6.34, -14.14) * mm, "mid": v(7.43, -13.6) * mm, "end": v(8.47, -12.98) * mm, "construction": true});
            skLineSegment(sketch, "E21", {"start": v(-15.5, 0) * mm, "end": v(15.5, 0) * mm, "construction": true});
            skLineSegment(sketch, "E22.0", {"start": v(-15.48, 0.75) * mm, "end": v(-3.93, 0.75) * mm});
            skArc(sketch, "E23", {"start": v(1, -3.87) * mm, "mid": v(2.03, -3.45) * mm, "end": v(2.9, -2.75) * mm});
            skLineSegment(sketch, "E24.0", {"start": v(-15.25, 2.75) * mm, "end": v(-2.9, 2.75) * mm});
            skLineSegment(sketch, "E25.0", {"start": v(-14.9, 4.25) * mm, "end": v(-1, 4.25) * mm});
            skLineSegment(sketch, "E26.0", {"start": v(-14.18, 6.25) * mm, "end": v(-1, 6.25) * mm});
            skLineSegment(sketch, "E27.0", {"start": v(-13.42, 7.75) * mm, "end": v(-1, 7.75) * mm});
            skLineSegment(sketch, "E28.0", {"start": v(-12.05, 9.75) * mm, "end": v(-1, 9.75) * mm});
            skLineSegment(sketch, "E29.0", {"start": v(-10.66, 11.25) * mm, "end": v(-1, 11.25) * mm});
            skLineSegment(sketch, "E30.0", {"start": v(-8.04, 13.25) * mm, "end": v(-1, 13.25) * mm});
            skLineSegment(sketch, "E31.0", {"start": v(-4.76, 14.75) * mm, "end": v(-1, 14.75) * mm});
            skLineSegment(sketch, "E32.trimOffspring", {"start": v(3.93, 0.75) * mm, "end": v(15.48, 0.75) * mm});
            skLineSegment(sketch, "E33.trimOffspring", {"start": v(2.9, 2.75) * mm, "end": v(15.25, 2.75) * mm});
            skLineSegment(sketch, "E34", {"start": v(0, 0) * mm, "end": v(0, 20) * mm, "construction": true});
            skLineSegment(sketch, "E35.0", {"start": v(1, 3.87) * mm, "end": v(1, 4.25) * mm});
            skLineSegment(sketch, "E36.0", {"start": v(-1, 3.87) * mm, "end": v(-1, 4.25) * mm});
            skLineSegment(sketch, "E37.MirrorCS", {"start": v(-15.48, -0.75) * mm, "end": v(-3.93, -0.75) * mm});
            skLineSegment(sketch, "E38.MirrorCS", {"start": v(-15.25, -2.75) * mm, "end": v(-2.9, -2.75) * mm});
            skLineSegment(sketch, "E39.MirrorCS", {"start": v(-14.9, -4.25) * mm, "end": v(-1, -4.25) * mm});
            skLineSegment(sketch, "E40.MirrorCS", {"start": v(-14.18, -6.25) * mm, "end": v(-1, -6.25) * mm});
            skLineSegment(sketch, "E41.MirrorCS", {"start": v(-13.42, -7.75) * mm, "end": v(-1, -7.75) * mm});
            skLineSegment(sketch, "E42.MirrorCS", {"start": v(-12.05, -9.75) * mm, "end": v(-1, -9.75) * mm});
            skLineSegment(sketch, "E43.MirrorCS", {"start": v(-10.66, -11.25) * mm, "end": v(-1, -11.25) * mm});
            skLineSegment(sketch, "E44.MirrorCS", {"start": v(-8.04, -13.25) * mm, "end": v(-1, -13.25) * mm});
            skLineSegment(sketch, "E45.MirrorCS", {"start": v(-4.76, -14.75) * mm, "end": v(-1, -14.75) * mm});
            skLineSegment(sketch, "E46.MirrorCS", {"start": v(-1, -3.87) * mm, "end": v(-1, -4.25) * mm});
            skLineSegment(sketch, "E47.MirrorCS", {"start": v(1, -3.87) * mm, "end": v(1, -4.25) * mm});
            skLineSegment(sketch, "E48.MirrorCS", {"start": v(3.93, -0.75) * mm, "end": v(15.48, -0.75) * mm});
            skLineSegment(sketch, "E49.MirrorCS", {"start": v(2.9, -2.75) * mm, "end": v(15.25, -2.75) * mm});
            skLineSegment(sketch, "E50.trimOffspring", {"start": v(1, -4.25) * mm, "end": v(14.9, -4.25) * mm});
            skLineSegment(sketch, "E51.trimOffspring", {"start": v(1, -6.25) * mm, "end": v(14.18, -6.25) * mm});
            skLineSegment(sketch, "E52.trimOffspring", {"start": v(1, -7.75) * mm, "end": v(13.42, -7.75) * mm});
            skLineSegment(sketch, "E53.trimOffspring", {"start": v(1, -9.75) * mm, "end": v(12.05, -9.75) * mm});
            skLineSegment(sketch, "E54.trimOffspring", {"start": v(1, -11.25) * mm, "end": v(10.66, -11.25) * mm});
            skLineSegment(sketch, "E55.trimOffspring", {"start": v(1, -13.25) * mm, "end": v(8.04, -13.25) * mm});
            skLineSegment(sketch, "E56.trimOffspring", {"start": v(1, -14.75) * mm, "end": v(4.76, -14.75) * mm});
            skArc(sketch, "E57.trimOffspring", {"start": v(-1, 3.87) * mm, "mid": v(-2.03, 3.45) * mm, "end": v(-2.9, 2.75) * mm});
            skLineSegment(sketch, "E58.trimOffspring", {"start": v(1, 4.25) * mm, "end": v(14.9, 4.25) * mm});
            skLineSegment(sketch, "E59.trimOffspring", {"start": v(1, 6.25) * mm, "end": v(14.18, 6.25) * mm});
            skLineSegment(sketch, "E60.trimOffspring", {"start": v(1, 7.75) * mm, "end": v(13.42, 7.75) * mm});
            skLineSegment(sketch, "E61.trimOffspring", {"start": v(1, 9.75) * mm, "end": v(12.05, 9.75) * mm});
            skLineSegment(sketch, "E62.trimOffspring", {"start": v(1, 11.25) * mm, "end": v(10.66, 11.25) * mm});
            skLineSegment(sketch, "E63.trimOffspring", {"start": v(1, 13.25) * mm, "end": v(8.04, 13.25) * mm});
            skLineSegment(sketch, "E64.trimOffspring", {"start": v(1, 14.75) * mm, "end": v(4.76, 14.75) * mm});
            skArc(sketch, "E65.trimOffspring", {"start": v(3.93, -0.75) * mm, "mid": v(4, 0) * mm, "end": v(3.93, 0.75) * mm});
            skArc(sketch, "E66.trimOffspring", {"start": v(2.9, 2.75) * mm, "mid": v(2.03, 3.45) * mm, "end": v(1, 3.87) * mm});
            skArc(sketch, "E67.trimOffspring", {"start": v(-3.93, 0.75) * mm, "mid": v(-4, 0) * mm, "end": v(-3.93, -0.75) * mm});
            skArc(sketch, "E68.trimOffspring", {"start": v(-2.9, -2.75) * mm, "mid": v(-2.03, -3.45) * mm, "end": v(-1, -3.87) * mm});
            skLineSegment(sketch, "E69.trimOffspring", {"start": v(-1, -6.25) * mm, "end": v(-1, -7.75) * mm});
            skLineSegment(sketch, "E70.trimOffspring", {"start": v(-1, -9.75) * mm, "end": v(-1, -11.25) * mm});
            skLineSegment(sketch, "E71.trimOffspring", {"start": v(-1, -13.25) * mm, "end": v(-1, -14.75) * mm});
            skPoint(sketch, "E72.orphan", {"position": v(-0.78, -15.48) * mm});
            skLineSegment(sketch, "E73.trimOffspring", {"start": v(1, -6.25) * mm, "end": v(1, -7.75) * mm});
            skLineSegment(sketch, "E74.trimOffspring", {"start": v(1, -9.75) * mm, "end": v(1, -11.25) * mm});
            skLineSegment(sketch, "E75.trimOffspring", {"start": v(1, -13.25) * mm, "end": v(1, -14.75) * mm});
            skPoint(sketch, "E76.orphan", {"position": v(0.77, -15.48) * mm});
            skArc(sketch, "E77.trimOffspring", {"start": v(-15.25, -2.75) * mm, "mid": v(-15.1, -3.5) * mm, "end": v(-14.9, -4.25) * mm});
            skArc(sketch, "E78.trimOffspring", {"start": v(-14.18, -6.25) * mm, "mid": v(-13.82, -7.01) * mm, "end": v(-13.42, -7.75) * mm});
            skArc(sketch, "E79.trimOffspring", {"start": v(-12.05, -9.75) * mm, "mid": v(-11.38, -10.52) * mm, "end": v(-10.66, -11.25) * mm});
            skArc(sketch, "E80.trimOffspring", {"start": v(-8.04, -13.25) * mm, "mid": v(-6.45, -14.1) * mm, "end": v(-4.76, -14.75) * mm});
            skArc(sketch, "E81.trimOffspring", {"start": v(-8.47, -12.98) * mm, "mid": v(-7.43, -13.6) * mm, "end": v(-6.34, -14.14) * mm, "construction": true});
            skArc(sketch, "E82.trimOffspring", {"start": v(4.76, -14.75) * mm, "mid": v(6.45, -14.1) * mm, "end": v(8.04, -13.25) * mm});
            skArc(sketch, "E83.trimOffspring", {"start": v(10.66, -11.25) * mm, "mid": v(11.38, -10.52) * mm, "end": v(12.05, -9.75) * mm});
            skArc(sketch, "E84.trimOffspring", {"start": v(13.42, -7.75) * mm, "mid": v(13.82, -7.01) * mm, "end": v(14.18, -6.25) * mm});
            skArc(sketch, "E85.trimOffspring", {"start": v(14.9, -4.25) * mm, "mid": v(15.1, -3.5) * mm, "end": v(15.25, -2.75) * mm});
            skArc(sketch, "E86.trimOffspring", {"start": v(15.48, -0.75) * mm, "mid": v(15.5, 0) * mm, "end": v(15.48, 0.75) * mm});
            skLineSegment(sketch, "E87.trimOffspring", {"start": v(1, 6.25) * mm, "end": v(1, 7.75) * mm});
            skLineSegment(sketch, "E88.trimOffspring", {"start": v(1, 9.75) * mm, "end": v(1, 11.25) * mm});
            skLineSegment(sketch, "E89.trimOffspring", {"start": v(1, 13.25) * mm, "end": v(1, 14.75) * mm});
            skPoint(sketch, "E90.orphan", {"position": v(0.77, 15.48) * mm});
            skArc(sketch, "E91.trimOffspring", {"start": v(8.04, 13.25) * mm, "mid": v(6.45, 14.1) * mm, "end": v(4.76, 14.75) * mm});
            skArc(sketch, "E92.trimOffspring", {"start": v(12.05, 9.75) * mm, "mid": v(11.38, 10.52) * mm, "end": v(10.66, 11.25) * mm});
            skArc(sketch, "E93.trimOffspring", {"start": v(14.18, 6.25) * mm, "mid": v(13.82, 7.01) * mm, "end": v(13.42, 7.75) * mm});
            skArc(sketch, "E94.trimOffspring", {"start": v(15.25, 2.75) * mm, "mid": v(15.1, 3.5) * mm, "end": v(14.9, 4.25) * mm});
            skLineSegment(sketch, "E95.trimOffspring", {"start": v(-1, 6.25) * mm, "end": v(-1, 7.75) * mm});
            skLineSegment(sketch, "E96.trimOffspring", {"start": v(-1, 9.75) * mm, "end": v(-1, 11.25) * mm});
            skLineSegment(sketch, "E97.trimOffspring", {"start": v(-1, 13.25) * mm, "end": v(-1, 14.75) * mm});
            skPoint(sketch, "E98.orphan", {"position": v(-0.78, 15.48) * mm});
            skArc(sketch, "E99.trimOffspring", {"start": v(-4.76, 14.75) * mm, "mid": v(-6.45, 14.1) * mm, "end": v(-8.04, 13.25) * mm});
            skArc(sketch, "E100.trimOffspring", {"start": v(-10.66, 11.25) * mm, "mid": v(-11.38, 10.52) * mm, "end": v(-12.05, 9.75) * mm});
            skArc(sketch, "E101.trimOffspring", {"start": v(-13.42, 7.75) * mm, "mid": v(-13.82, 7.01) * mm, "end": v(-14.18, 6.25) * mm});
            skArc(sketch, "E102.trimOffspring", {"start": v(-14.9, 4.25) * mm, "mid": v(-15.1, 3.5) * mm, "end": v(-15.25, 2.75) * mm});
            skArc(sketch, "E103.trimOffspring", {"start": v(-15.48, 0.75) * mm, "mid": v(-15.5, 0) * mm, "end": v(-15.48, -0.75) * mm});
            skSolve(sketch);
        }
        {
            var Q0;
            Q0 = qSketchRegion(id + "F10", true);
            extrude(context, id + "F11", {"entities" : qUnion([Q0]), "operationType" : NewBodyOperationType.REMOVE, "oppositeDirection" : true, "depth" : 10 * mm, "offsetDistance" : 25 * mm});
        }
        {
            var Q0;
            Q0=makeQuery(id+"F1.opRevolve","SWEPT_EDGE",EDGE,{"disambiguationData":[OSD([sQuery(id+"F0.wireOp",EDGE,"E9.0"),sQuery(id+"F0.wireOp",EDGE,"E10")])]});
            chamfer(context, id + "F12", {"entities" : qUnion([Q0]), "width" : 0.5 * mm, "tangentPropagation" : true});
        }
    });
